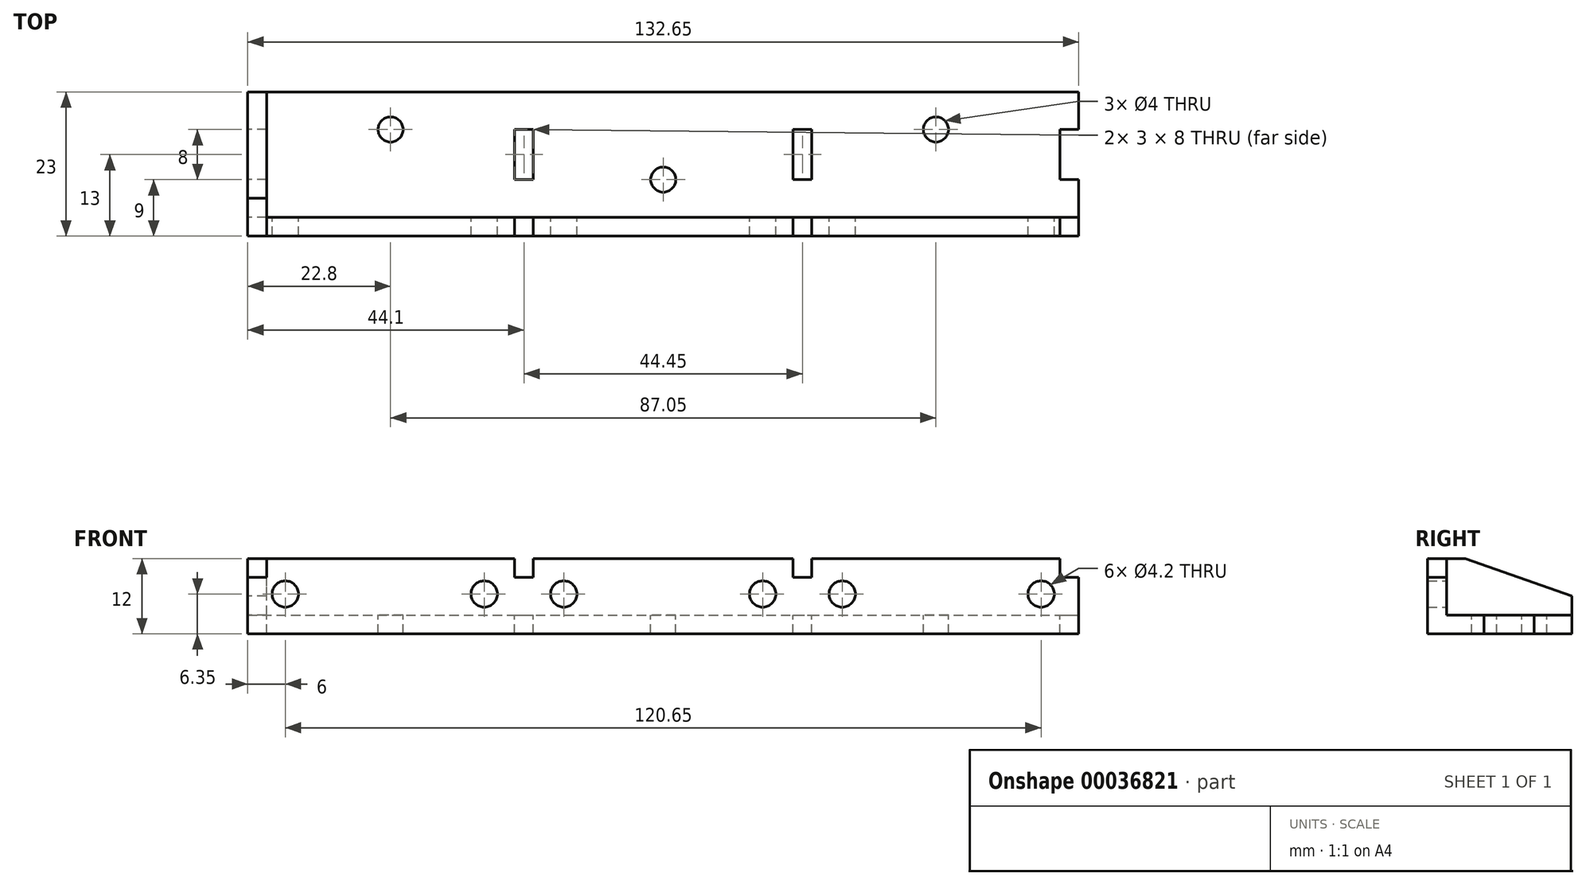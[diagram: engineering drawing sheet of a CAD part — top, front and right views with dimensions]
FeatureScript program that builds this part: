
annotation { "Feature Type Name" : "Feature", "Feature Type Description" : "" }
export const myFeature = defineFeature(function(context is Context, id is Id, definition is map)
    precondition{}
    {
        {
            var Q0;
            Q0=qCreatedBy(makeId("Front.planeOp"),FACE);
            var sketch = newSketch(context, id + "F0", { "sketchPlane" : qUnion([Q0])});
            skLineSegment(sketch, "E0.bottom", {"start": v(0, 0) * mm, "end": v(132.65, 0) * mm});
            skLineSegment(sketch, "E0.top", {"start": v(0, 12) * mm, "end": v(132.65, 12) * mm});
            skLineSegment(sketch, "E0.left", {"start": v(0, 0) * mm, "end": v(0, 12) * mm});
            skCircle(sketch, "E1", {"center": v(6, 6.35) * mm, "radius": 2.1 * mm});
            skCircle(sketch, "E2", {"center": v(37.75, 6.35) * mm, "radius": 2.1 * mm});
            skCircle(sketch, "E3", {"center": v(50.45, 6.35) * mm, "radius": 2.1 * mm});
            skCircle(sketch, "E4", {"center": v(82.2, 6.35) * mm, "radius": 2.1 * mm});
            skCircle(sketch, "E5", {"center": v(94.9, 6.35) * mm, "radius": 2.1 * mm});
            skCircle(sketch, "E6", {"center": v(126.65, 6.35) * mm, "radius": 2.1 * mm});
            skLineSegment(sketch, "E7", {"start": v(6, 6.35) * mm, "end": v(37.75, 6.35) * mm, "construction": true});
            skLineSegment(sketch, "E8", {"start": v(50.45, 6.35) * mm, "end": v(82.2, 6.35) * mm, "construction": true});
            skLineSegment(sketch, "E9", {"start": v(94.9, 6.35) * mm, "end": v(126.65, 6.35) * mm, "construction": true});
            skLineSegment(sketch, "E10", {"start": v(37.75, 6.35) * mm, "end": v(50.45, 6.35) * mm, "construction": true});
            skLineSegment(sketch, "E11", {"start": v(82.2, 6.35) * mm, "end": v(94.9, 6.35) * mm, "construction": true});
            skLineSegment(sketch, "E12", {"start": v(6, 6.35) * mm, "end": v(0, 6.35) * mm, "construction": true});
            skPoint(sketch, "E13", {"position": v(44.1, 6.35) * mm});
            skPoint(sketch, "E14", {"position": v(88.55, 6.35) * mm});
            skCircle(sketch, "E15", {"center": v(50.45, 6.35) * mm, "radius": 2.5 * mm, "construction": true});
            skLineSegment(sketch, "E16", {"start": v(132.65, 12) * mm, "end": v(132.65, 0) * mm});
            skLineSegment(sketch, "E17", {"start": v(126.65, 6.35) * mm, "end": v(132.65, 6.35) * mm, "construction": true});
            skSolve(sketch);
        }
        {
            var Q0;
            Q0=makeQuery(id+"F0.imprint","IMPRINT",FACE,{"disambiguationData":[TD([[makeQuery(id+"F0.imprint","IMPRINT",EDGE,{"derivedFrom":sQuery(id+"F0.wireOp",EDGE,"E0.bottom")}),1.0]])]});
            var sketch = newSketch(context, id + "F1", { "sketchPlane" : qUnion([Q0])});
            skLineSegment(sketch, "E18.bottom", {"start": v(6, 0) * mm, "end": v(9, 0) * mm});
            skLineSegment(sketch, "E18.top", {"start": v(6, 3) * mm, "end": v(9, 3) * mm});
            skLineSegment(sketch, "E18.left", {"start": v(6, 0) * mm, "end": v(6, 3) * mm});
            skLineSegment(sketch, "E18.right", {"start": v(9, 0) * mm, "end": v(9, 3) * mm});
            skLineSegment(sketch, "E19.bottom", {"start": v(11.75, 0) * mm, "end": v(14.75, 0) * mm});
            skLineSegment(sketch, "E19.top", {"start": v(11.75, 3) * mm, "end": v(14.75, 3) * mm});
            skLineSegment(sketch, "E19.left", {"start": v(11.75, 0) * mm, "end": v(11.75, 3) * mm});
            skLineSegment(sketch, "E19.right", {"start": v(14.75, 0) * mm, "end": v(14.75, 3) * mm});
            skLineSegment(sketch, "E20.bottom", {"start": v(17.5, 0) * mm, "end": v(20.5, 0) * mm});
            skLineSegment(sketch, "E20.top", {"start": v(17.5, 3) * mm, "end": v(20.5, 3) * mm});
            skLineSegment(sketch, "E20.left", {"start": v(17.5, 0) * mm, "end": v(17.5, 3) * mm});
            skLineSegment(sketch, "E20.right", {"start": v(20.5, 0) * mm, "end": v(20.5, 3) * mm});
            skLineSegment(sketch, "E21", {"start": v(9, 3) * mm, "end": v(11.75, 3) * mm, "construction": true});
            skLineSegment(sketch, "E22", {"start": v(14.75, 3) * mm, "end": v(17.5, 3) * mm, "construction": true});
            skLineSegment(sketch, "E23.bottom", {"start": v(23.25, 0) * mm, "end": v(26.25, 0) * mm});
            skLineSegment(sketch, "E23.top", {"start": v(23.25, 3) * mm, "end": v(26.25, 3) * mm});
            skLineSegment(sketch, "E23.left", {"start": v(23.25, 0) * mm, "end": v(23.25, 3) * mm});
            skLineSegment(sketch, "E23.right", {"start": v(26.25, 0) * mm, "end": v(26.25, 3) * mm});
            skLineSegment(sketch, "E24.bottom", {"start": v(29, 0) * mm, "end": v(32, 0) * mm});
            skLineSegment(sketch, "E24.top", {"start": v(29, 3) * mm, "end": v(32, 3) * mm});
            skLineSegment(sketch, "E24.left", {"start": v(29, 0) * mm, "end": v(29, 3) * mm});
            skLineSegment(sketch, "E24.right", {"start": v(32, 0) * mm, "end": v(32, 3) * mm});
            skLineSegment(sketch, "E25.bottom", {"start": v(34.75, 0) * mm, "end": v(37.75, 0) * mm});
            skLineSegment(sketch, "E25.top", {"start": v(34.75, 3) * mm, "end": v(37.75, 3) * mm});
            skLineSegment(sketch, "E25.left", {"start": v(34.75, 0) * mm, "end": v(34.75, 3) * mm});
            skLineSegment(sketch, "E25.right", {"start": v(37.75, 0) * mm, "end": v(37.75, 3) * mm});
            skLineSegment(sketch, "E26", {"start": v(20.5, 3) * mm, "end": v(23.25, 3) * mm, "construction": true});
            skLineSegment(sketch, "E27", {"start": v(26.25, 3) * mm, "end": v(29, 3) * mm, "construction": true});
            skLineSegment(sketch, "E28", {"start": v(32, 3) * mm, "end": v(34.75, 3) * mm, "construction": true});
            skLineSegment(sketch, "E29", {"start": v(44.1, 6.35) * mm, "end": v(44.1, 0) * mm, "construction": true});
            skLineSegment(sketch, "E30.MirrorCS", {"start": v(61.95, 3) * mm, "end": v(59.2, 3) * mm, "construction": true});
            skLineSegment(sketch, "E31.MirrorCS", {"start": v(76.45, 0) * mm, "end": v(73.45, 0) * mm});
            skLineSegment(sketch, "E32.MirrorCS", {"start": v(50.45, 0) * mm, "end": v(50.45, 3) * mm});
            skLineSegment(sketch, "E33.MirrorCS", {"start": v(53.45, 0) * mm, "end": v(53.45, 3) * mm});
            skLineSegment(sketch, "E34.MirrorCS", {"start": v(61.95, 0) * mm, "end": v(61.95, 3) * mm});
            skLineSegment(sketch, "E35.MirrorCS", {"start": v(79.2, 3) * mm, "end": v(76.45, 3) * mm, "construction": true});
            skLineSegment(sketch, "E36.MirrorCS", {"start": v(70.7, 0) * mm, "end": v(70.7, 3) * mm});
            skLineSegment(sketch, "E37.MirrorCS", {"start": v(59.2, 3) * mm, "end": v(56.2, 3) * mm});
            skLineSegment(sketch, "E38.MirrorCS", {"start": v(67.7, 0) * mm, "end": v(67.7, 3) * mm});
            skLineSegment(sketch, "E39.MirrorCS", {"start": v(64.95, 0) * mm, "end": v(64.95, 3) * mm});
            skLineSegment(sketch, "E40.MirrorCS", {"start": v(67.7, 3) * mm, "end": v(64.95, 3) * mm, "construction": true});
            skLineSegment(sketch, "E41.MirrorCS", {"start": v(82.2, 0) * mm, "end": v(79.2, 0) * mm});
            skLineSegment(sketch, "E42.MirrorCS", {"start": v(64.95, 0) * mm, "end": v(61.95, 0) * mm});
            skLineSegment(sketch, "E43.MirrorCS", {"start": v(53.45, 0) * mm, "end": v(50.45, 0) * mm});
            skLineSegment(sketch, "E44.MirrorCS", {"start": v(73.45, 0) * mm, "end": v(73.45, 3) * mm});
            skLineSegment(sketch, "E45.MirrorCS", {"start": v(82.2, 0) * mm, "end": v(82.2, 3) * mm});
            skLineSegment(sketch, "E46.MirrorCS", {"start": v(56.2, 0) * mm, "end": v(56.2, 3) * mm});
            skLineSegment(sketch, "E47.MirrorCS", {"start": v(53.45, 3) * mm, "end": v(50.45, 3) * mm});
            skLineSegment(sketch, "E48.MirrorCS", {"start": v(64.95, 3) * mm, "end": v(61.95, 3) * mm});
            skLineSegment(sketch, "E49.MirrorCS", {"start": v(59.2, 0) * mm, "end": v(56.2, 0) * mm});
            skLineSegment(sketch, "E50.MirrorCS", {"start": v(70.7, 3) * mm, "end": v(67.7, 3) * mm});
            skLineSegment(sketch, "E51.MirrorCS", {"start": v(70.7, 0) * mm, "end": v(67.7, 0) * mm});
            skLineSegment(sketch, "E52.MirrorCS", {"start": v(76.45, 3) * mm, "end": v(73.45, 3) * mm});
            skLineSegment(sketch, "E53.MirrorCS", {"start": v(56.2, 3) * mm, "end": v(53.45, 3) * mm, "construction": true});
            skLineSegment(sketch, "E54.MirrorCS", {"start": v(73.45, 3) * mm, "end": v(70.7, 3) * mm, "construction": true});
            skLineSegment(sketch, "E55.MirrorCS", {"start": v(79.2, 0) * mm, "end": v(79.2, 3) * mm});
            skLineSegment(sketch, "E56.MirrorCS", {"start": v(82.2, 3) * mm, "end": v(79.2, 3) * mm});
            skLineSegment(sketch, "E57.MirrorCS", {"start": v(59.2, 0) * mm, "end": v(59.2, 3) * mm});
            skLineSegment(sketch, "E58.MirrorCS", {"start": v(76.45, 0) * mm, "end": v(76.45, 3) * mm});
            skLineSegment(sketch, "E59", {"start": v(88.55, 6.35) * mm, "end": v(88.55, 0) * mm, "construction": true});
            skLineSegment(sketch, "E60.MirrorCS", {"start": v(97.9, 3) * mm, "end": v(100.65, 3) * mm, "construction": true});
            skLineSegment(sketch, "E61.MirrorCS", {"start": v(106.4, 3) * mm, "end": v(109.4, 3) * mm});
            skLineSegment(sketch, "E62.MirrorCS", {"start": v(109.4, 3) * mm, "end": v(112.15, 3) * mm, "construction": true});
            skLineSegment(sketch, "E63.MirrorCS", {"start": v(115.15, 3) * mm, "end": v(117.9, 3) * mm, "construction": true});
            skLineSegment(sketch, "E64.MirrorCS", {"start": v(103.65, 3) * mm, "end": v(106.4, 3) * mm, "construction": true});
            skLineSegment(sketch, "E65.MirrorCS", {"start": v(100.65, 3) * mm, "end": v(103.65, 3) * mm});
            skLineSegment(sketch, "E66.MirrorCS", {"start": v(112.15, 3) * mm, "end": v(115.15, 3) * mm});
            skLineSegment(sketch, "E67.MirrorCS", {"start": v(120.9, 3) * mm, "end": v(123.65, 3) * mm, "construction": true});
            skLineSegment(sketch, "E68.MirrorCS", {"start": v(117.9, 3) * mm, "end": v(120.9, 3) * mm});
            skLineSegment(sketch, "E69.MirrorCS", {"start": v(106.4, 0) * mm, "end": v(109.4, 0) * mm});
            skLineSegment(sketch, "E70.MirrorCS", {"start": v(112.15, 0) * mm, "end": v(115.15, 0) * mm});
            skLineSegment(sketch, "E71.MirrorCS", {"start": v(100.65, 0) * mm, "end": v(100.65, 3) * mm});
            skLineSegment(sketch, "E72.MirrorCS", {"start": v(115.15, 0) * mm, "end": v(115.15, 3) * mm});
            skLineSegment(sketch, "E73.MirrorCS", {"start": v(94.9, 0) * mm, "end": v(97.9, 0) * mm});
            skLineSegment(sketch, "E74.MirrorCS", {"start": v(117.9, 0) * mm, "end": v(117.9, 3) * mm});
            skLineSegment(sketch, "E75.MirrorCS", {"start": v(123.65, 0) * mm, "end": v(123.65, 3) * mm});
            skLineSegment(sketch, "E76.MirrorCS", {"start": v(117.9, 0) * mm, "end": v(120.9, 0) * mm});
            skLineSegment(sketch, "E77.MirrorCS", {"start": v(94.9, 3) * mm, "end": v(97.9, 3) * mm});
            skLineSegment(sketch, "E78.MirrorCS", {"start": v(120.9, 0) * mm, "end": v(120.9, 3) * mm});
            skLineSegment(sketch, "E79.MirrorCS", {"start": v(94.9, 0) * mm, "end": v(94.9, 3) * mm});
            skLineSegment(sketch, "E80.MirrorCS", {"start": v(126.65, 0) * mm, "end": v(126.65, 3) * mm});
            skLineSegment(sketch, "E81.MirrorCS", {"start": v(112.15, 0) * mm, "end": v(112.15, 3) * mm});
            skLineSegment(sketch, "E82.MirrorCS", {"start": v(123.65, 3) * mm, "end": v(126.65, 3) * mm});
            skLineSegment(sketch, "E83.MirrorCS", {"start": v(106.4, 0) * mm, "end": v(106.4, 3) * mm});
            skLineSegment(sketch, "E84.MirrorCS", {"start": v(97.9, 0) * mm, "end": v(97.9, 3) * mm});
            skLineSegment(sketch, "E85.MirrorCS", {"start": v(123.65, 0) * mm, "end": v(126.65, 0) * mm});
            skLineSegment(sketch, "E86.MirrorCS", {"start": v(103.65, 0) * mm, "end": v(103.65, 3) * mm});
            skLineSegment(sketch, "E87.MirrorCS", {"start": v(100.65, 0) * mm, "end": v(103.65, 0) * mm});
            skLineSegment(sketch, "E88.MirrorCS", {"start": v(109.4, 0) * mm, "end": v(109.4, 3) * mm});
            skLineSegment(sketch, "E89.bottom", {"start": v(0, 0) * mm, "end": v(3, 0) * mm});
            skLineSegment(sketch, "E89.top", {"start": v(0, 3) * mm, "end": v(3, 3) * mm});
            skLineSegment(sketch, "E89.left", {"start": v(0, 0) * mm, "end": v(0, 3) * mm});
            skLineSegment(sketch, "E89.right", {"start": v(3, 0) * mm, "end": v(3, 3) * mm});
            skLineSegment(sketch, "E90.bottom", {"start": v(42.6, 0) * mm, "end": v(45.6, 0) * mm});
            skLineSegment(sketch, "E90.top", {"start": v(42.6, 3) * mm, "end": v(45.6, 3) * mm});
            skLineSegment(sketch, "E90.left", {"start": v(42.6, 0) * mm, "end": v(42.6, 3) * mm});
            skLineSegment(sketch, "E90.right", {"start": v(45.6, 0) * mm, "end": v(45.6, 3) * mm});
            skLineSegment(sketch, "E91.bottom", {"start": v(87.05, 0) * mm, "end": v(90.05, 0) * mm});
            skLineSegment(sketch, "E91.top", {"start": v(87.05, 3) * mm, "end": v(90.05, 3) * mm});
            skLineSegment(sketch, "E91.left", {"start": v(87.05, 0) * mm, "end": v(87.05, 3) * mm});
            skLineSegment(sketch, "E91.right", {"start": v(90.05, 0) * mm, "end": v(90.05, 3) * mm});
            skPoint(sketch, "E92", {"position": v(44.1, 0) * mm});
            skPoint(sketch, "E93", {"position": v(88.55, 0) * mm});
            skLineSegment(sketch, "E94.bottom", {"start": v(132.65, 0) * mm, "end": v(129.65, 0) * mm});
            skLineSegment(sketch, "E94.top", {"start": v(132.65, 3) * mm, "end": v(129.65, 3) * mm});
            skLineSegment(sketch, "E94.left", {"start": v(132.65, 0) * mm, "end": v(132.65, 3) * mm});
            skLineSegment(sketch, "E94.right", {"start": v(129.65, 0) * mm, "end": v(129.65, 3) * mm});
            skSolve(sketch);
        }
        {
            var Q0;
            Q0=qCreatedBy(makeId("Front.planeOp"),FACE);
            var sketch = newSketch(context, id + "F2", { "sketchPlane" : qUnion([Q0])});
            skLineSegment(sketch, "E95.bottom", {"start": v(0, 0) * mm, "end": v(132.65, 0) * mm});
            skLineSegment(sketch, "E95.top", {"start": v(0, 3) * mm, "end": v(132.65, 3) * mm});
            skLineSegment(sketch, "E95.left", {"start": v(0, 0) * mm, "end": v(0, 3) * mm});
            skLineSegment(sketch, "E95.right", {"start": v(132.65, 0) * mm, "end": v(132.65, 3) * mm});
            skSolve(sketch);
        }
        {
            var Q0;
            Q0=qSketchRegion(id+"F0",true);
            extrude(context, id + "F3", {"entities" : qUnion([Q0]), "depth" : 3 * mm});
        }
        {
            var Q0;
            Q0=makeQuery(id+"F1.imprint","IMPRINT",FACE,{"disambiguationData":[TD([[makeQuery(id+"F1.imprint","IMPRINT",EDGE,{"derivedFrom":sQuery(id+"F1.wireOp",EDGE,"E89.bottom")}),1.0]])]});
            var Q1;
            Q1=makeQuery(id+"F1.imprint","IMPRINT",FACE,{"disambiguationData":[TD([[makeQuery(id+"F1.imprint","IMPRINT",EDGE,{"derivedFrom":sQuery(id+"F1.wireOp",EDGE,"E18.bottom")}),1.0]])]});
            var Q2;
            Q2=makeQuery(id+"F1.imprint","IMPRINT",FACE,{"disambiguationData":[TD([[makeQuery(id+"F1.imprint","IMPRINT",EDGE,{"derivedFrom":sQuery(id+"F1.wireOp",EDGE,"E19.bottom")}),1.0]])]});
            var Q3;
            Q3=makeQuery(id+"F1.imprint","IMPRINT",FACE,{"disambiguationData":[TD([[makeQuery(id+"F1.imprint","IMPRINT",EDGE,{"derivedFrom":sQuery(id+"F1.wireOp",EDGE,"E20.bottom")}),1.0]])]});
            var Q4;
            Q4=makeQuery(id+"F1.imprint","IMPRINT",FACE,{"disambiguationData":[TD([[makeQuery(id+"F1.imprint","IMPRINT",EDGE,{"derivedFrom":sQuery(id+"F1.wireOp",EDGE,"E23.bottom")}),1.0]])]});
            var Q5;
            Q5=makeQuery(id+"F1.imprint","IMPRINT",FACE,{"disambiguationData":[TD([[makeQuery(id+"F1.imprint","IMPRINT",EDGE,{"derivedFrom":sQuery(id+"F1.wireOp",EDGE,"E24.bottom")}),1.0]])]});
            var Q6;
            Q6=makeQuery(id+"F1.imprint","IMPRINT",FACE,{"disambiguationData":[TD([[makeQuery(id+"F1.imprint","IMPRINT",EDGE,{"derivedFrom":sQuery(id+"F1.wireOp",EDGE,"E25.bottom")}),1.0]])]});
            var Q7;
            Q7=makeQuery(id+"F1.imprint","IMPRINT",FACE,{"disambiguationData":[TD([[makeQuery(id+"F1.imprint","IMPRINT",EDGE,{"derivedFrom":sQuery(id+"F1.wireOp",EDGE,"E90.bottom")}),1.0]])]});
            var Q8;
            Q8=makeQuery(id+"F1.imprint","IMPRINT",FACE,{"disambiguationData":[TD([[makeQuery(id+"F1.imprint","IMPRINT",EDGE,{"derivedFrom":sQuery(id+"F1.wireOp",EDGE,"E32.MirrorCS")}),-1.0]])]});
            var Q9;
            Q9=makeQuery(id+"F1.imprint","IMPRINT",FACE,{"disambiguationData":[TD([[makeQuery(id+"F1.imprint","IMPRINT",EDGE,{"derivedFrom":sQuery(id+"F1.wireOp",EDGE,"E37.MirrorCS")}),1.0]])]});
            var Q10;
            Q10=makeQuery(id+"F1.imprint","IMPRINT",FACE,{"disambiguationData":[TD([[makeQuery(id+"F1.imprint","IMPRINT",EDGE,{"derivedFrom":sQuery(id+"F1.wireOp",EDGE,"E34.MirrorCS")}),-1.0]])]});
            var Q11;
            Q11=makeQuery(id+"F1.imprint","IMPRINT",FACE,{"disambiguationData":[TD([[makeQuery(id+"F1.imprint","IMPRINT",EDGE,{"derivedFrom":sQuery(id+"F1.wireOp",EDGE,"E36.MirrorCS")}),1.0]])]});
            var Q12;
            Q12=makeQuery(id+"F1.imprint","IMPRINT",FACE,{"disambiguationData":[TD([[makeQuery(id+"F1.imprint","IMPRINT",EDGE,{"derivedFrom":sQuery(id+"F1.wireOp",EDGE,"E31.MirrorCS")}),1.0]])]});
            var Q13;
            Q13=makeQuery(id+"F1.imprint","IMPRINT",FACE,{"disambiguationData":[TD([[makeQuery(id+"F1.imprint","IMPRINT",EDGE,{"derivedFrom":sQuery(id+"F1.wireOp",EDGE,"E41.MirrorCS")}),1.0]])]});
            var Q14;
            Q14=makeQuery(id+"F1.imprint","IMPRINT",FACE,{"disambiguationData":[TD([[makeQuery(id+"F1.imprint","IMPRINT",EDGE,{"derivedFrom":sQuery(id+"F1.wireOp",EDGE,"E91.bottom")}),1.0]])]});
            var Q15;
            Q15=makeQuery(id+"F1.imprint","IMPRINT",FACE,{"disambiguationData":[TD([[makeQuery(id+"F1.imprint","IMPRINT",EDGE,{"derivedFrom":sQuery(id+"F1.wireOp",EDGE,"E73.MirrorCS")}),1.0]])]});
            var Q16;
            Q16=makeQuery(id+"F1.imprint","IMPRINT",FACE,{"disambiguationData":[TD([[makeQuery(id+"F1.imprint","IMPRINT",EDGE,{"derivedFrom":sQuery(id+"F1.wireOp",EDGE,"E65.MirrorCS")}),-1.0]])]});
            var Q17;
            Q17=makeQuery(id+"F1.imprint","IMPRINT",FACE,{"disambiguationData":[TD([[makeQuery(id+"F1.imprint","IMPRINT",EDGE,{"derivedFrom":sQuery(id+"F1.wireOp",EDGE,"E61.MirrorCS")}),-1.0]])]});
            var Q18;
            Q18=makeQuery(id+"F1.imprint","IMPRINT",FACE,{"disambiguationData":[TD([[makeQuery(id+"F1.imprint","IMPRINT",EDGE,{"derivedFrom":sQuery(id+"F1.wireOp",EDGE,"E66.MirrorCS")}),-1.0]])]});
            var Q19;
            Q19=makeQuery(id+"F1.imprint","IMPRINT",FACE,{"disambiguationData":[TD([[makeQuery(id+"F1.imprint","IMPRINT",EDGE,{"derivedFrom":sQuery(id+"F1.wireOp",EDGE,"E68.MirrorCS")}),-1.0]])]});
            var Q20;
            Q20=makeQuery(id+"F1.imprint","IMPRINT",FACE,{"disambiguationData":[TD([[makeQuery(id+"F1.imprint","IMPRINT",EDGE,{"derivedFrom":sQuery(id+"F1.wireOp",EDGE,"E75.MirrorCS")}),-1.0]])]});
            var Q21;
            Q21=makeQuery(id+"F1.imprint","IMPRINT",FACE,{"disambiguationData":[TD([[makeQuery(id+"F1.imprint","IMPRINT",EDGE,{"derivedFrom":sQuery(id+"F1.wireOp",EDGE,"d6889f29-3aff-4a43-887b-f05846102f70.bottom")}),1.0]])]});
            var Q22;
            Q22=makeQuery(id+"F1.imprint","IMPRINT",FACE,{"disambiguationData":[TD([[makeQuery(id+"F1.imprint","IMPRINT",EDGE,{"derivedFrom":sQuery(id+"F1.wireOp",EDGE,"3edb70b5-b804-4be9-ab85-b3a438d2129227.MirrorCS")}),1.0]])]});
            var Q23;
            Q23=makeQuery(id+"F1.imprint","IMPRINT",FACE,{"disambiguationData":[TD([[makeQuery(id+"F1.imprint","IMPRINT",EDGE,{"derivedFrom":sQuery(id+"F1.wireOp",EDGE,"3edb70b5-b804-4be9-ab85-b3a438d212923.MirrorCS")}),1.0]])]});
            var Q24;
            Q24=makeQuery(id+"F1.imprint","IMPRINT",FACE,{"disambiguationData":[TD([[makeQuery(id+"F1.imprint","IMPRINT",EDGE,{"derivedFrom":sQuery(id+"F1.wireOp",EDGE,"3edb70b5-b804-4be9-ab85-b3a438d2129214.MirrorCS")}),1.0]])]});
            var Q25;
            Q25=makeQuery(id+"F1.imprint","IMPRINT",FACE,{"disambiguationData":[TD([[makeQuery(id+"F1.imprint","IMPRINT",EDGE,{"derivedFrom":sQuery(id+"F1.wireOp",EDGE,"3edb70b5-b804-4be9-ab85-b3a438d212922.MirrorCS")}),1.0]])]});
            var Q26;
            Q26=makeQuery(id+"F1.imprint","IMPRINT",FACE,{"disambiguationData":[TD([[makeQuery(id+"F1.imprint","IMPRINT",EDGE,{"derivedFrom":sQuery(id+"F1.wireOp",EDGE,"3edb70b5-b804-4be9-ab85-b3a438d2129216.MirrorCS")}),1.0]])]});
            var Q27;
            Q27=makeQuery(id+"F1.imprint","IMPRINT",FACE,{"disambiguationData":[TD([[makeQuery(id+"F1.imprint","IMPRINT",EDGE,{"derivedFrom":sQuery(id+"F1.wireOp",EDGE,"3edb70b5-b804-4be9-ab85-b3a438d2129232.MirrorCS")}),-1.0]])]});
            var Q28;
            {var subQ3=sQuery(id+"F1.wireOp",EDGE,"767c3735-2e18-495c-a88c-5e601239b8bc.left");Q28=makeQuery(id+"F1.imprint","IMPRINT",FACE,{"disambiguationData":[TD([[makeQuery(id+"F1.imprint","IMPRINT",EDGE,{"derivedFrom":subQ3}),-1.0]])]});}
            var Q29;
            {var subQ0=sQuery(id+"F1.wireOp",EDGE,"767c3735-2e18-495c-a88c-5e601239b8bc.right");Q29=makeQuery(id+"F1.imprint","IMPRINT",FACE,{"disambiguationData":[TD([[makeQuery(id+"F1.imprint","IMPRINT",EDGE,{"derivedFrom":subQ0}),1.0]])]});}
            var Q30;
            Q30=makeQuery(id+"F1.imprint","IMPRINT",FACE,{"disambiguationData":[TD([[makeQuery(id+"F1.imprint","IMPRINT",EDGE,{"derivedFrom":sQuery(id+"F1.wireOp",EDGE,"3edb70b5-b804-4be9-ab85-b3a438d2129229.MirrorCS")}),-1.0]])]});
            var Q31;
            Q31=makeQuery(id+"F1.imprint","IMPRINT",FACE,{"disambiguationData":[TD([[makeQuery(id+"F1.imprint","IMPRINT",EDGE,{"derivedFrom":sQuery(id+"F1.wireOp",EDGE,"3edb70b5-b804-4be9-ab85-b3a438d212921.MirrorCS")}),-1.0]])]});
            var Q32;
            Q32=makeQuery(id+"F1.imprint","IMPRINT",FACE,{"disambiguationData":[TD([[makeQuery(id+"F1.imprint","IMPRINT",EDGE,{"derivedFrom":sQuery(id+"F1.wireOp",EDGE,"3edb70b5-b804-4be9-ab85-b3a438d2129215.MirrorCS")}),-1.0]])]});
            var Q33;
            Q33=makeQuery(id+"F1.imprint","IMPRINT",FACE,{"disambiguationData":[TD([[makeQuery(id+"F1.imprint","IMPRINT",EDGE,{"derivedFrom":sQuery(id+"F1.wireOp",EDGE,"3edb70b5-b804-4be9-ab85-b3a438d2129220.MirrorCS")}),-1.0]])]});
            var Q34;
            Q34=makeQuery(id+"F1.imprint","IMPRINT",FACE,{"disambiguationData":[TD([[makeQuery(id+"F1.imprint","IMPRINT",EDGE,{"derivedFrom":sQuery(id+"F1.wireOp",EDGE,"3edb70b5-b804-4be9-ab85-b3a438d212927.MirrorCS")}),-1.0]])]});
            var Q35;
            Q35=makeQuery(id+"F1.imprint","IMPRINT",FACE,{"disambiguationData":[TD([[makeQuery(id+"F1.imprint","IMPRINT",EDGE,{"derivedFrom":sQuery(id+"F1.wireOp",EDGE,"3edb70b5-b804-4be9-ab85-b3a438d2129228.MirrorCS")}),1.0]])]});
            var Q36;
            {var subQ3=sQuery(id+"F1.wireOp",EDGE,"543f3bcf-fd4b-4987-a5e7-407be729de0d0.MirrorCS");Q36=makeQuery(id+"F1.imprint","IMPRINT",FACE,{"disambiguationData":[TD([[makeQuery(id+"F1.imprint","IMPRINT",EDGE,{"derivedFrom":subQ3}),-1.0]])]});}
            var Q37;
            {var subQ1=sQuery(id+"F1.wireOp",EDGE,"ccf9539e-e2bb-4c1d-8ae2-5d85fc4c74a40.MirrorCS");Q37=makeQuery(id+"F1.imprint","IMPRINT",FACE,{"disambiguationData":[TD([[makeQuery(id+"F1.imprint","IMPRINT",EDGE,{"derivedFrom":subQ1}),1.0]])]});}
            var Q38;
            Q38=makeQuery(id+"F1.imprint","IMPRINT",FACE,{"disambiguationData":[TD([[makeQuery(id+"F1.imprint","IMPRINT",EDGE,{"derivedFrom":sQuery(id+"F1.wireOp",EDGE,"3edb70b5-b804-4be9-ab85-b3a438d2129251.MirrorCS")}),-1.0]])]});
            var Q39;
            Q39=makeQuery(id+"F1.imprint","IMPRINT",FACE,{"disambiguationData":[TD([[makeQuery(id+"F1.imprint","IMPRINT",EDGE,{"derivedFrom":sQuery(id+"F1.wireOp",EDGE,"3edb70b5-b804-4be9-ab85-b3a438d2129211.MirrorCS")}),1.0]])]});
            var Q40;
            Q40=makeQuery(id+"F1.imprint","IMPRINT",FACE,{"disambiguationData":[TD([[makeQuery(id+"F1.imprint","IMPRINT",EDGE,{"derivedFrom":sQuery(id+"F1.wireOp",EDGE,"3edb70b5-b804-4be9-ab85-b3a438d2129226.MirrorCS")}),1.0]])]});
            var Q41;
            Q41=makeQuery(id+"F1.imprint","IMPRINT",FACE,{"disambiguationData":[TD([[makeQuery(id+"F1.imprint","IMPRINT",EDGE,{"derivedFrom":sQuery(id+"F1.wireOp",EDGE,"3edb70b5-b804-4be9-ab85-b3a438d2129218.MirrorCS")}),1.0]])]});
            var Q42;
            Q42=makeQuery(id+"F1.imprint","IMPRINT",FACE,{"disambiguationData":[TD([[makeQuery(id+"F1.imprint","IMPRINT",EDGE,{"derivedFrom":sQuery(id+"F1.wireOp",EDGE,"3edb70b5-b804-4be9-ab85-b3a438d2129225.MirrorCS")}),1.0]])]});
            var Q43;
            Q43=makeQuery(id+"F1.imprint","IMPRINT",FACE,{"disambiguationData":[TD([[makeQuery(id+"F1.imprint","IMPRINT",EDGE,{"derivedFrom":sQuery(id+"F1.wireOp",EDGE,"3edb70b5-b804-4be9-ab85-b3a438d2129263.MirrorCS")}),-1.0]])]});
            var Q44;
            Q44=makeQuery(id+"F1.imprint","IMPRINT",FACE,{"disambiguationData":[TD([[makeQuery(id+"F1.imprint","IMPRINT",EDGE,{"derivedFrom":sQuery(id+"F1.wireOp",EDGE,"6148efe5-7769-4a6e-beb2-6f02e7a2884e0.MirrorCS")}),1.0]])]});
            var Q45;
            Q45=makeQuery(id+"F1.imprint","IMPRINT",FACE,{"disambiguationData":[TD([[makeQuery(id+"F1.imprint","IMPRINT",EDGE,{"derivedFrom":sQuery(id+"F1.wireOp",EDGE,"14cc3a12-7d66-4c02-94a9-419769d5725533.MirrorCS")}),-1.0]])]});
            var Q46;
            Q46=makeQuery(id+"F1.imprint","IMPRINT",FACE,{"disambiguationData":[TD([[makeQuery(id+"F1.imprint","IMPRINT",EDGE,{"derivedFrom":sQuery(id+"F1.wireOp",EDGE,"14cc3a12-7d66-4c02-94a9-419769d572550.MirrorCS")}),-1.0]])]});
            var Q47;
            Q47=makeQuery(id+"F1.imprint","IMPRINT",FACE,{"disambiguationData":[TD([[makeQuery(id+"F1.imprint","IMPRINT",EDGE,{"derivedFrom":sQuery(id+"F1.wireOp",EDGE,"14cc3a12-7d66-4c02-94a9-419769d572558.MirrorCS")}),-1.0]])]});
            var Q48;
            Q48=makeQuery(id+"F1.imprint","IMPRINT",FACE,{"disambiguationData":[TD([[makeQuery(id+"F1.imprint","IMPRINT",EDGE,{"derivedFrom":sQuery(id+"F1.wireOp",EDGE,"14cc3a12-7d66-4c02-94a9-419769d5725514.MirrorCS")}),-1.0]])]});
            var Q49;
            Q49=makeQuery(id+"F1.imprint","IMPRINT",FACE,{"disambiguationData":[TD([[makeQuery(id+"F1.imprint","IMPRINT",EDGE,{"derivedFrom":sQuery(id+"F1.wireOp",EDGE,"14cc3a12-7d66-4c02-94a9-419769d5725517.MirrorCS")}),-1.0]])]});
            var Q50;
            Q50=makeQuery(id+"F1.imprint","IMPRINT",FACE,{"disambiguationData":[TD([[makeQuery(id+"F1.imprint","IMPRINT",EDGE,{"derivedFrom":sQuery(id+"F1.wireOp",EDGE,"14cc3a12-7d66-4c02-94a9-419769d5725522.MirrorCS")}),-1.0]])]});
            var Q51;
            {var subQ1=sQuery(id+"F1.wireOp",EDGE,"64f74f13-c9d3-42ce-b6e6-9e83b05c69170.MirrorCS");Q51=makeQuery(id+"F1.imprint","IMPRINT",FACE,{"disambiguationData":[TD([[makeQuery(id+"F1.imprint","IMPRINT",EDGE,{"derivedFrom":subQ1}),-1.0]])]});}
            var Q52;
            {var subQ3=sQuery(id+"F1.wireOp",EDGE,"b25d534e-4642-4852-ae6d-545176e5d0d50.MirrorCS");Q52=makeQuery(id+"F1.imprint","IMPRINT",FACE,{"disambiguationData":[TD([[makeQuery(id+"F1.imprint","IMPRINT",EDGE,{"derivedFrom":subQ3}),1.0]])]});}
            var Q53;
            Q53=makeQuery(id+"F1.imprint","IMPRINT",FACE,{"disambiguationData":[TD([[makeQuery(id+"F1.imprint","IMPRINT",EDGE,{"derivedFrom":sQuery(id+"F1.wireOp",EDGE,"14cc3a12-7d66-4c02-94a9-419769d5725521.MirrorCS")}),1.0]])]});
            var Q54;
            Q54=makeQuery(id+"F1.imprint","IMPRINT",FACE,{"disambiguationData":[TD([[makeQuery(id+"F1.imprint","IMPRINT",EDGE,{"derivedFrom":sQuery(id+"F1.wireOp",EDGE,"14cc3a12-7d66-4c02-94a9-419769d572553.MirrorCS")}),1.0]])]});
            var Q55;
            Q55=makeQuery(id+"F1.imprint","IMPRINT",FACE,{"disambiguationData":[TD([[makeQuery(id+"F1.imprint","IMPRINT",EDGE,{"derivedFrom":sQuery(id+"F1.wireOp",EDGE,"14cc3a12-7d66-4c02-94a9-419769d572557.MirrorCS")}),1.0]])]});
            var Q56;
            Q56=makeQuery(id+"F1.imprint","IMPRINT",FACE,{"disambiguationData":[TD([[makeQuery(id+"F1.imprint","IMPRINT",EDGE,{"derivedFrom":sQuery(id+"F1.wireOp",EDGE,"14cc3a12-7d66-4c02-94a9-419769d5725512.MirrorCS")}),1.0]])]});
            var Q57;
            Q57=makeQuery(id+"F1.imprint","IMPRINT",FACE,{"disambiguationData":[TD([[makeQuery(id+"F1.imprint","IMPRINT",EDGE,{"derivedFrom":sQuery(id+"F1.wireOp",EDGE,"14cc3a12-7d66-4c02-94a9-419769d5725515.MirrorCS")}),1.0]])]});
            var Q58;
            Q58=makeQuery(id+"F1.imprint","IMPRINT",FACE,{"disambiguationData":[TD([[makeQuery(id+"F1.imprint","IMPRINT",EDGE,{"derivedFrom":sQuery(id+"F1.wireOp",EDGE,"14cc3a12-7d66-4c02-94a9-419769d5725527.MirrorCS")}),-1.0]])]});
            var Q59;
            Q59=makeQuery(id+"F1.imprint","IMPRINT",FACE,{"disambiguationData":[TD([[makeQuery(id+"F1.imprint","IMPRINT",EDGE,{"derivedFrom":sQuery(id+"F1.wireOp",EDGE,"2b8ea9ff-144e-4082-a664-a4dd3dd94e410.MirrorCS")}),1.0]])]});
            var Q60;
            {var subQ2=sQuery(id+"F1.wireOp",EDGE,"SqbHijmA-EvCf-u65W-CcwQ-tsmZO2ZK6Ml2");Q60=makeQuery(id+"F1.imprint","IMPRINT",FACE,{"disambiguationData":[TD([[makeQuery(id+"F1.imprint","IMPRINT",EDGE,{"derivedFrom":subQ2}),1.0]])]});}
            extrude(context, id + "F4", {"entities" : qUnion([Q0, Q1, Q2, Q3, Q4, Q5, Q6, Q7, Q8, Q9, Q10, Q11, Q12, Q13, Q14, Q15, Q16, Q17, Q18, Q19, Q20, Q21, Q22, Q23, Q24, Q25, Q26, Q27, Q28, Q29, Q30, Q31, Q32, Q33, Q34, Q35, Q36, Q37, Q38, Q39, Q40, Q41, Q42, Q43, Q44, Q45, Q46, Q47, Q48, Q49, Q50, Q51, Q52, Q53, Q54, Q55, Q56, Q57, Q58, Q59, Q60]), "operationType" : NewBodyOperationType.REMOVE, "endBound" : BoundingType.THROUGH_ALL, "depth" : 25 * mm});
        }
        {
            var Q0;
            Q0=makeQuery(id+"F2.imprint","IMPRINT",FACE,{"disambiguationData":[TD([[makeQuery(id+"F2.imprint","IMPRINT",EDGE,{"derivedFrom":sQuery(id+"F2.wireOp",EDGE,"E95.bottom")}),1.0]])]});
            extrude(context, id + "F5", {"entities" : qUnion([Q0]), "oppositeDirection" : true, "depth" : 20 * mm});
        }
        {
            var Q0;
            Q0=makeQuery(id+"F1.imprint","IMPRINT",FACE,{"disambiguationData":[TD([[makeQuery(id+"F1.imprint","IMPRINT",EDGE,{"derivedFrom":sQuery(id+"F1.wireOp",EDGE,"2b8ea9ff-144e-4082-a664-a4dd3dd94e410.MirrorCS")}),1.0]])]});
            var Q1;
            Q1=makeQuery(id+"F1.imprint","IMPRINT",FACE,{"disambiguationData":[TD([[makeQuery(id+"F1.imprint","IMPRINT",EDGE,{"derivedFrom":sQuery(id+"F1.wireOp",EDGE,"14cc3a12-7d66-4c02-94a9-419769d5725527.MirrorCS")}),-1.0]])]});
            var Q2;
            Q2=makeQuery(id+"F1.imprint","IMPRINT",FACE,{"disambiguationData":[TD([[makeQuery(id+"F1.imprint","IMPRINT",EDGE,{"derivedFrom":sQuery(id+"F1.wireOp",EDGE,"14cc3a12-7d66-4c02-94a9-419769d5725515.MirrorCS")}),1.0]])]});
            var Q3;
            Q3=makeQuery(id+"F1.imprint","IMPRINT",FACE,{"disambiguationData":[TD([[makeQuery(id+"F1.imprint","IMPRINT",EDGE,{"derivedFrom":sQuery(id+"F1.wireOp",EDGE,"14cc3a12-7d66-4c02-94a9-419769d5725512.MirrorCS")}),1.0]])]});
            var Q4;
            Q4=makeQuery(id+"F1.imprint","IMPRINT",FACE,{"disambiguationData":[TD([[makeQuery(id+"F1.imprint","IMPRINT",EDGE,{"derivedFrom":sQuery(id+"F1.wireOp",EDGE,"14cc3a12-7d66-4c02-94a9-419769d572557.MirrorCS")}),1.0]])]});
            var Q5;
            Q5=makeQuery(id+"F1.imprint","IMPRINT",FACE,{"disambiguationData":[TD([[makeQuery(id+"F1.imprint","IMPRINT",EDGE,{"derivedFrom":sQuery(id+"F1.wireOp",EDGE,"14cc3a12-7d66-4c02-94a9-419769d572553.MirrorCS")}),1.0]])]});
            var Q6;
            Q6=makeQuery(id+"F1.imprint","IMPRINT",FACE,{"disambiguationData":[TD([[makeQuery(id+"F1.imprint","IMPRINT",EDGE,{"derivedFrom":sQuery(id+"F1.wireOp",EDGE,"14cc3a12-7d66-4c02-94a9-419769d5725521.MirrorCS")}),1.0]])]});
            var Q7;
            {var subQ3=sQuery(id+"F1.wireOp",EDGE,"b25d534e-4642-4852-ae6d-545176e5d0d50.MirrorCS");Q7=makeQuery(id+"F1.imprint","IMPRINT",FACE,{"disambiguationData":[TD([[makeQuery(id+"F1.imprint","IMPRINT",EDGE,{"derivedFrom":subQ3}),1.0]])]});}
            var Q8;
            {var subQ1=sQuery(id+"F1.wireOp",EDGE,"64f74f13-c9d3-42ce-b6e6-9e83b05c69170.MirrorCS");Q8=makeQuery(id+"F1.imprint","IMPRINT",FACE,{"disambiguationData":[TD([[makeQuery(id+"F1.imprint","IMPRINT",EDGE,{"derivedFrom":subQ1}),-1.0]])]});}
            var Q9;
            Q9=makeQuery(id+"F1.imprint","IMPRINT",FACE,{"disambiguationData":[TD([[makeQuery(id+"F1.imprint","IMPRINT",EDGE,{"derivedFrom":sQuery(id+"F1.wireOp",EDGE,"14cc3a12-7d66-4c02-94a9-419769d5725522.MirrorCS")}),-1.0]])]});
            var Q10;
            Q10=makeQuery(id+"F1.imprint","IMPRINT",FACE,{"disambiguationData":[TD([[makeQuery(id+"F1.imprint","IMPRINT",EDGE,{"derivedFrom":sQuery(id+"F1.wireOp",EDGE,"14cc3a12-7d66-4c02-94a9-419769d5725517.MirrorCS")}),-1.0]])]});
            var Q11;
            Q11=makeQuery(id+"F1.imprint","IMPRINT",FACE,{"disambiguationData":[TD([[makeQuery(id+"F1.imprint","IMPRINT",EDGE,{"derivedFrom":sQuery(id+"F1.wireOp",EDGE,"14cc3a12-7d66-4c02-94a9-419769d5725514.MirrorCS")}),-1.0]])]});
            var Q12;
            Q12=makeQuery(id+"F1.imprint","IMPRINT",FACE,{"disambiguationData":[TD([[makeQuery(id+"F1.imprint","IMPRINT",EDGE,{"derivedFrom":sQuery(id+"F1.wireOp",EDGE,"14cc3a12-7d66-4c02-94a9-419769d572558.MirrorCS")}),-1.0]])]});
            var Q13;
            Q13=makeQuery(id+"F1.imprint","IMPRINT",FACE,{"disambiguationData":[TD([[makeQuery(id+"F1.imprint","IMPRINT",EDGE,{"derivedFrom":sQuery(id+"F1.wireOp",EDGE,"14cc3a12-7d66-4c02-94a9-419769d572550.MirrorCS")}),-1.0]])]});
            var Q14;
            Q14=makeQuery(id+"F1.imprint","IMPRINT",FACE,{"disambiguationData":[TD([[makeQuery(id+"F1.imprint","IMPRINT",EDGE,{"derivedFrom":sQuery(id+"F1.wireOp",EDGE,"14cc3a12-7d66-4c02-94a9-419769d5725533.MirrorCS")}),-1.0]])]});
            var Q15;
            Q15=makeQuery(id+"F1.imprint","IMPRINT",FACE,{"disambiguationData":[TD([[makeQuery(id+"F1.imprint","IMPRINT",EDGE,{"derivedFrom":sQuery(id+"F1.wireOp",EDGE,"6148efe5-7769-4a6e-beb2-6f02e7a2884e0.MirrorCS")}),1.0]])]});
            var Q16;
            Q16=makeQuery(id+"F1.imprint","IMPRINT",FACE,{"disambiguationData":[TD([[makeQuery(id+"F1.imprint","IMPRINT",EDGE,{"derivedFrom":sQuery(id+"F1.wireOp",EDGE,"3edb70b5-b804-4be9-ab85-b3a438d2129263.MirrorCS")}),-1.0]])]});
            var Q17;
            Q17=makeQuery(id+"F1.imprint","IMPRINT",FACE,{"disambiguationData":[TD([[makeQuery(id+"F1.imprint","IMPRINT",EDGE,{"derivedFrom":sQuery(id+"F1.wireOp",EDGE,"3edb70b5-b804-4be9-ab85-b3a438d2129225.MirrorCS")}),1.0]])]});
            var Q18;
            Q18=makeQuery(id+"F1.imprint","IMPRINT",FACE,{"disambiguationData":[TD([[makeQuery(id+"F1.imprint","IMPRINT",EDGE,{"derivedFrom":sQuery(id+"F1.wireOp",EDGE,"3edb70b5-b804-4be9-ab85-b3a438d2129218.MirrorCS")}),1.0]])]});
            var Q19;
            Q19=makeQuery(id+"F1.imprint","IMPRINT",FACE,{"disambiguationData":[TD([[makeQuery(id+"F1.imprint","IMPRINT",EDGE,{"derivedFrom":sQuery(id+"F1.wireOp",EDGE,"3edb70b5-b804-4be9-ab85-b3a438d2129226.MirrorCS")}),1.0]])]});
            var Q20;
            Q20=makeQuery(id+"F1.imprint","IMPRINT",FACE,{"disambiguationData":[TD([[makeQuery(id+"F1.imprint","IMPRINT",EDGE,{"derivedFrom":sQuery(id+"F1.wireOp",EDGE,"3edb70b5-b804-4be9-ab85-b3a438d2129211.MirrorCS")}),1.0]])]});
            var Q21;
            Q21=makeQuery(id+"F1.imprint","IMPRINT",FACE,{"disambiguationData":[TD([[makeQuery(id+"F1.imprint","IMPRINT",EDGE,{"derivedFrom":sQuery(id+"F1.wireOp",EDGE,"3edb70b5-b804-4be9-ab85-b3a438d2129251.MirrorCS")}),-1.0]])]});
            var Q22;
            {var subQ1=sQuery(id+"F1.wireOp",EDGE,"ccf9539e-e2bb-4c1d-8ae2-5d85fc4c74a40.MirrorCS");Q22=makeQuery(id+"F1.imprint","IMPRINT",FACE,{"disambiguationData":[TD([[makeQuery(id+"F1.imprint","IMPRINT",EDGE,{"derivedFrom":subQ1}),1.0]])]});}
            var Q23;
            {var subQ3=sQuery(id+"F1.wireOp",EDGE,"543f3bcf-fd4b-4987-a5e7-407be729de0d0.MirrorCS");Q23=makeQuery(id+"F1.imprint","IMPRINT",FACE,{"disambiguationData":[TD([[makeQuery(id+"F1.imprint","IMPRINT",EDGE,{"derivedFrom":subQ3}),-1.0]])]});}
            var Q24;
            Q24=makeQuery(id+"F1.imprint","IMPRINT",FACE,{"disambiguationData":[TD([[makeQuery(id+"F1.imprint","IMPRINT",EDGE,{"derivedFrom":sQuery(id+"F1.wireOp",EDGE,"3edb70b5-b804-4be9-ab85-b3a438d2129228.MirrorCS")}),1.0]])]});
            var Q25;
            Q25=makeQuery(id+"F1.imprint","IMPRINT",FACE,{"disambiguationData":[TD([[makeQuery(id+"F1.imprint","IMPRINT",EDGE,{"derivedFrom":sQuery(id+"F1.wireOp",EDGE,"3edb70b5-b804-4be9-ab85-b3a438d212927.MirrorCS")}),-1.0]])]});
            var Q26;
            Q26=makeQuery(id+"F1.imprint","IMPRINT",FACE,{"disambiguationData":[TD([[makeQuery(id+"F1.imprint","IMPRINT",EDGE,{"derivedFrom":sQuery(id+"F1.wireOp",EDGE,"3edb70b5-b804-4be9-ab85-b3a438d2129220.MirrorCS")}),-1.0]])]});
            var Q27;
            Q27=makeQuery(id+"F1.imprint","IMPRINT",FACE,{"disambiguationData":[TD([[makeQuery(id+"F1.imprint","IMPRINT",EDGE,{"derivedFrom":sQuery(id+"F1.wireOp",EDGE,"3edb70b5-b804-4be9-ab85-b3a438d2129215.MirrorCS")}),-1.0]])]});
            var Q28;
            Q28=makeQuery(id+"F1.imprint","IMPRINT",FACE,{"disambiguationData":[TD([[makeQuery(id+"F1.imprint","IMPRINT",EDGE,{"derivedFrom":sQuery(id+"F1.wireOp",EDGE,"3edb70b5-b804-4be9-ab85-b3a438d212921.MirrorCS")}),-1.0]])]});
            var Q29;
            Q29=makeQuery(id+"F1.imprint","IMPRINT",FACE,{"disambiguationData":[TD([[makeQuery(id+"F1.imprint","IMPRINT",EDGE,{"derivedFrom":sQuery(id+"F1.wireOp",EDGE,"3edb70b5-b804-4be9-ab85-b3a438d2129229.MirrorCS")}),-1.0]])]});
            var Q30;
            {var subQ0=sQuery(id+"F1.wireOp",EDGE,"767c3735-2e18-495c-a88c-5e601239b8bc.right");Q30=makeQuery(id+"F1.imprint","IMPRINT",FACE,{"disambiguationData":[TD([[makeQuery(id+"F1.imprint","IMPRINT",EDGE,{"derivedFrom":subQ0}),1.0]])]});}
            var Q31;
            {var subQ3=sQuery(id+"F1.wireOp",EDGE,"767c3735-2e18-495c-a88c-5e601239b8bc.left");Q31=makeQuery(id+"F1.imprint","IMPRINT",FACE,{"disambiguationData":[TD([[makeQuery(id+"F1.imprint","IMPRINT",EDGE,{"derivedFrom":subQ3}),-1.0]])]});}
            var Q32;
            Q32=makeQuery(id+"F1.imprint","IMPRINT",FACE,{"disambiguationData":[TD([[makeQuery(id+"F1.imprint","IMPRINT",EDGE,{"derivedFrom":sQuery(id+"F1.wireOp",EDGE,"3edb70b5-b804-4be9-ab85-b3a438d2129232.MirrorCS")}),-1.0]])]});
            var Q33;
            Q33=makeQuery(id+"F1.imprint","IMPRINT",FACE,{"disambiguationData":[TD([[makeQuery(id+"F1.imprint","IMPRINT",EDGE,{"derivedFrom":sQuery(id+"F1.wireOp",EDGE,"3edb70b5-b804-4be9-ab85-b3a438d2129216.MirrorCS")}),1.0]])]});
            var Q34;
            Q34=makeQuery(id+"F1.imprint","IMPRINT",FACE,{"disambiguationData":[TD([[makeQuery(id+"F1.imprint","IMPRINT",EDGE,{"derivedFrom":sQuery(id+"F1.wireOp",EDGE,"3edb70b5-b804-4be9-ab85-b3a438d212922.MirrorCS")}),1.0]])]});
            var Q35;
            Q35=makeQuery(id+"F1.imprint","IMPRINT",FACE,{"disambiguationData":[TD([[makeQuery(id+"F1.imprint","IMPRINT",EDGE,{"derivedFrom":sQuery(id+"F1.wireOp",EDGE,"3edb70b5-b804-4be9-ab85-b3a438d2129214.MirrorCS")}),1.0]])]});
            var Q36;
            Q36=makeQuery(id+"F1.imprint","IMPRINT",FACE,{"disambiguationData":[TD([[makeQuery(id+"F1.imprint","IMPRINT",EDGE,{"derivedFrom":sQuery(id+"F1.wireOp",EDGE,"3edb70b5-b804-4be9-ab85-b3a438d212923.MirrorCS")}),1.0]])]});
            var Q37;
            Q37=makeQuery(id+"F1.imprint","IMPRINT",FACE,{"disambiguationData":[TD([[makeQuery(id+"F1.imprint","IMPRINT",EDGE,{"derivedFrom":sQuery(id+"F1.wireOp",EDGE,"3edb70b5-b804-4be9-ab85-b3a438d2129227.MirrorCS")}),1.0]])]});
            var Q38;
            Q38=makeQuery(id+"F1.imprint","IMPRINT",FACE,{"disambiguationData":[TD([[makeQuery(id+"F1.imprint","IMPRINT",EDGE,{"derivedFrom":sQuery(id+"F1.wireOp",EDGE,"E75.MirrorCS")}),-1.0]])]});
            var Q39;
            Q39=makeQuery(id+"F1.imprint","IMPRINT",FACE,{"disambiguationData":[TD([[makeQuery(id+"F1.imprint","IMPRINT",EDGE,{"derivedFrom":sQuery(id+"F1.wireOp",EDGE,"E68.MirrorCS")}),-1.0]])]});
            var Q40;
            Q40=makeQuery(id+"F1.imprint","IMPRINT",FACE,{"disambiguationData":[TD([[makeQuery(id+"F1.imprint","IMPRINT",EDGE,{"derivedFrom":sQuery(id+"F1.wireOp",EDGE,"E66.MirrorCS")}),-1.0]])]});
            var Q41;
            Q41=makeQuery(id+"F1.imprint","IMPRINT",FACE,{"disambiguationData":[TD([[makeQuery(id+"F1.imprint","IMPRINT",EDGE,{"derivedFrom":sQuery(id+"F1.wireOp",EDGE,"E61.MirrorCS")}),-1.0]])]});
            var Q42;
            Q42=makeQuery(id+"F1.imprint","IMPRINT",FACE,{"disambiguationData":[TD([[makeQuery(id+"F1.imprint","IMPRINT",EDGE,{"derivedFrom":sQuery(id+"F1.wireOp",EDGE,"E65.MirrorCS")}),-1.0]])]});
            var Q43;
            Q43=makeQuery(id+"F1.imprint","IMPRINT",FACE,{"disambiguationData":[TD([[makeQuery(id+"F1.imprint","IMPRINT",EDGE,{"derivedFrom":sQuery(id+"F1.wireOp",EDGE,"E73.MirrorCS")}),1.0]])]});
            var Q44;
            Q44=makeQuery(id+"F1.imprint","IMPRINT",FACE,{"disambiguationData":[TD([[makeQuery(id+"F1.imprint","IMPRINT",EDGE,{"derivedFrom":sQuery(id+"F1.wireOp",EDGE,"d6889f29-3aff-4a43-887b-f05846102f70.bottom")}),1.0]])]});
            var Q45;
            Q45=makeQuery(id+"F1.imprint","IMPRINT",FACE,{"disambiguationData":[TD([[makeQuery(id+"F1.imprint","IMPRINT",EDGE,{"derivedFrom":sQuery(id+"F1.wireOp",EDGE,"E91.bottom")}),1.0]])]});
            var Q46;
            Q46=makeQuery(id+"F1.imprint","IMPRINT",FACE,{"disambiguationData":[TD([[makeQuery(id+"F1.imprint","IMPRINT",EDGE,{"derivedFrom":sQuery(id+"F1.wireOp",EDGE,"E41.MirrorCS")}),1.0]])]});
            var Q47;
            Q47=makeQuery(id+"F1.imprint","IMPRINT",FACE,{"disambiguationData":[TD([[makeQuery(id+"F1.imprint","IMPRINT",EDGE,{"derivedFrom":sQuery(id+"F1.wireOp",EDGE,"E31.MirrorCS")}),1.0]])]});
            var Q48;
            Q48=makeQuery(id+"F1.imprint","IMPRINT",FACE,{"disambiguationData":[TD([[makeQuery(id+"F1.imprint","IMPRINT",EDGE,{"derivedFrom":sQuery(id+"F1.wireOp",EDGE,"E36.MirrorCS")}),1.0]])]});
            var Q49;
            Q49=makeQuery(id+"F1.imprint","IMPRINT",FACE,{"disambiguationData":[TD([[makeQuery(id+"F1.imprint","IMPRINT",EDGE,{"derivedFrom":sQuery(id+"F1.wireOp",EDGE,"E34.MirrorCS")}),-1.0]])]});
            var Q50;
            Q50=makeQuery(id+"F1.imprint","IMPRINT",FACE,{"disambiguationData":[TD([[makeQuery(id+"F1.imprint","IMPRINT",EDGE,{"derivedFrom":sQuery(id+"F1.wireOp",EDGE,"E37.MirrorCS")}),1.0]])]});
            var Q51;
            Q51=makeQuery(id+"F1.imprint","IMPRINT",FACE,{"disambiguationData":[TD([[makeQuery(id+"F1.imprint","IMPRINT",EDGE,{"derivedFrom":sQuery(id+"F1.wireOp",EDGE,"E32.MirrorCS")}),-1.0]])]});
            var Q52;
            Q52=makeQuery(id+"F1.imprint","IMPRINT",FACE,{"disambiguationData":[TD([[makeQuery(id+"F1.imprint","IMPRINT",EDGE,{"derivedFrom":sQuery(id+"F1.wireOp",EDGE,"E90.bottom")}),1.0]])]});
            var Q53;
            Q53=makeQuery(id+"F1.imprint","IMPRINT",FACE,{"disambiguationData":[TD([[makeQuery(id+"F1.imprint","IMPRINT",EDGE,{"derivedFrom":sQuery(id+"F1.wireOp",EDGE,"E25.bottom")}),1.0]])]});
            var Q54;
            Q54=makeQuery(id+"F1.imprint","IMPRINT",FACE,{"disambiguationData":[TD([[makeQuery(id+"F1.imprint","IMPRINT",EDGE,{"derivedFrom":sQuery(id+"F1.wireOp",EDGE,"E24.bottom")}),1.0]])]});
            var Q55;
            Q55=makeQuery(id+"F1.imprint","IMPRINT",FACE,{"disambiguationData":[TD([[makeQuery(id+"F1.imprint","IMPRINT",EDGE,{"derivedFrom":sQuery(id+"F1.wireOp",EDGE,"E23.bottom")}),1.0]])]});
            var Q56;
            Q56=makeQuery(id+"F1.imprint","IMPRINT",FACE,{"disambiguationData":[TD([[makeQuery(id+"F1.imprint","IMPRINT",EDGE,{"derivedFrom":sQuery(id+"F1.wireOp",EDGE,"E20.bottom")}),1.0]])]});
            var Q57;
            Q57=makeQuery(id+"F1.imprint","IMPRINT",FACE,{"disambiguationData":[TD([[makeQuery(id+"F1.imprint","IMPRINT",EDGE,{"derivedFrom":sQuery(id+"F1.wireOp",EDGE,"E19.bottom")}),1.0]])]});
            var Q58;
            Q58=makeQuery(id+"F1.imprint","IMPRINT",FACE,{"disambiguationData":[TD([[makeQuery(id+"F1.imprint","IMPRINT",EDGE,{"derivedFrom":sQuery(id+"F1.wireOp",EDGE,"E18.bottom")}),1.0]])]});
            var Q59;
            Q59=makeQuery(id+"F1.imprint","IMPRINT",FACE,{"disambiguationData":[TD([[makeQuery(id+"F1.imprint","IMPRINT",EDGE,{"derivedFrom":sQuery(id+"F1.wireOp",EDGE,"E89.bottom")}),1.0]])]});
            var Q60;
            Q60=makeQuery(id+"F1.imprint","IMPRINT",FACE,{"disambiguationData":[TD([[makeQuery(id+"F1.imprint","IMPRINT",EDGE,{"derivedFrom":sQuery(id+"F1.wireOp",EDGE,"E94.bottom")}),1.0]])]});
            extrude(context, id + "F6", {"entities" : qUnion([Q0, Q1, Q2, Q3, Q4, Q5, Q6, Q7, Q8, Q9, Q10, Q11, Q12, Q13, Q14, Q15, Q16, Q17, Q18, Q19, Q20, Q21, Q22, Q23, Q24, Q25, Q26, Q27, Q28, Q29, Q30, Q31, Q32, Q33, Q34, Q35, Q36, Q37, Q38, Q39, Q40, Q41, Q42, Q43, Q44, Q45, Q46, Q47, Q48, Q49, Q50, Q51, Q52, Q53, Q54, Q55, Q56, Q57, Q58, Q59, Q60]), "operationType" : NewBodyOperationType.ADD, "depth" : 3 * mm});
        }
        {
            var Q0;
            Q0=makeQuery(id+"F6.boolean.opBoolean","MERGE",FACE,{"derivedFrom":[makeQuery(id+"F5.opExtrude","SWEPT_FACE",FACE,{"disambiguationData":[OSD([sQuery(id+"F2.wireOp",EDGE,"E95.top")])]}),makeQuery(id+"F6.opExtrude","SWEPT_FACE",FACE,{"disambiguationData":[OSD([sQuery(id+"F1.wireOp",EDGE,"E18.top")])]}),makeQuery(id+"F6.opExtrude","SWEPT_FACE",FACE,{"disambiguationData":[OSD([sQuery(id+"F1.wireOp",EDGE,"E19.top")])]}),makeQuery(id+"F6.opExtrude","SWEPT_FACE",FACE,{"disambiguationData":[OSD([sQuery(id+"F1.wireOp",EDGE,"E20.top")])]}),makeQuery(id+"F6.opExtrude","SWEPT_FACE",FACE,{"disambiguationData":[OSD([sQuery(id+"F1.wireOp",EDGE,"E23.top")])]}),makeQuery(id+"F6.opExtrude","SWEPT_FACE",FACE,{"disambiguationData":[OSD([sQuery(id+"F1.wireOp",EDGE,"E24.top")])]}),makeQuery(id+"F6.opExtrude","SWEPT_FACE",FACE,{"disambiguationData":[OSD([sQuery(id+"F1.wireOp",EDGE,"E25.top")])]}),makeQuery(id+"F6.opExtrude","SWEPT_FACE",FACE,{"disambiguationData":[OSD([sQuery(id+"F1.wireOp",EDGE,"E37.MirrorCS")])]}),makeQuery(id+"F6.opExtrude","SWEPT_FACE",FACE,{"disambiguationData":[OSD([sQuery(id+"F1.wireOp",EDGE,"E47.MirrorCS")])]}),makeQuery(id+"F6.opExtrude","SWEPT_FACE",FACE,{"disambiguationData":[OSD([sQuery(id+"F1.wireOp",EDGE,"E48.MirrorCS")])]}),makeQuery(id+"F6.opExtrude","SWEPT_FACE",FACE,{"disambiguationData":[OSD([sQuery(id+"F1.wireOp",EDGE,"E50.MirrorCS")])]}),makeQuery(id+"F6.opExtrude","SWEPT_FACE",FACE,{"disambiguationData":[OSD([sQuery(id+"F1.wireOp",EDGE,"E52.MirrorCS")])]}),makeQuery(id+"F6.opExtrude","SWEPT_FACE",FACE,{"disambiguationData":[OSD([sQuery(id+"F1.wireOp",EDGE,"E56.MirrorCS")])]}),makeQuery(id+"F6.opExtrude","SWEPT_FACE",FACE,{"disambiguationData":[OSD([sQuery(id+"F1.wireOp",EDGE,"E61.MirrorCS")])]}),makeQuery(id+"F6.opExtrude","SWEPT_FACE",FACE,{"disambiguationData":[OSD([sQuery(id+"F1.wireOp",EDGE,"E65.MirrorCS")])]}),makeQuery(id+"F6.opExtrude","SWEPT_FACE",FACE,{"disambiguationData":[OSD([sQuery(id+"F1.wireOp",EDGE,"E66.MirrorCS")])]}),makeQuery(id+"F6.opExtrude","SWEPT_FACE",FACE,{"disambiguationData":[OSD([sQuery(id+"F1.wireOp",EDGE,"E68.MirrorCS")])]}),makeQuery(id+"F6.opExtrude","SWEPT_FACE",FACE,{"disambiguationData":[OSD([sQuery(id+"F1.wireOp",EDGE,"E77.MirrorCS")])]}),makeQuery(id+"F6.opExtrude","SWEPT_FACE",FACE,{"disambiguationData":[OSD([sQuery(id+"F1.wireOp",EDGE,"E82.MirrorCS")])]}),makeQuery(id+"F6.opExtrude","SWEPT_FACE",FACE,{"disambiguationData":[OSD([sQuery(id+"F1.wireOp",EDGE,"3edb70b5-b804-4be9-ab85-b3a438d212921.MirrorCS")])]}),makeQuery(id+"F6.opExtrude","SWEPT_FACE",FACE,{"disambiguationData":[OSD([sQuery(id+"F1.wireOp",EDGE,"3edb70b5-b804-4be9-ab85-b3a438d212922.MirrorCS")])]}),makeQuery(id+"F6.opExtrude","SWEPT_FACE",FACE,{"disambiguationData":[OSD([sQuery(id+"F1.wireOp",EDGE,"3edb70b5-b804-4be9-ab85-b3a438d212923.MirrorCS")])]}),makeQuery(id+"F6.opExtrude","SWEPT_FACE",FACE,{"disambiguationData":[OSD([sQuery(id+"F1.wireOp",EDGE,"3edb70b5-b804-4be9-ab85-b3a438d212927.MirrorCS")])]}),makeQuery(id+"F6.opExtrude","SWEPT_FACE",FACE,{"disambiguationData":[OSD([sQuery(id+"F1.wireOp",EDGE,"3edb70b5-b804-4be9-ab85-b3a438d2129211.MirrorCS")])]}),makeQuery(id+"F6.opExtrude","SWEPT_FACE",FACE,{"disambiguationData":[OSD([sQuery(id+"F1.wireOp",EDGE,"3edb70b5-b804-4be9-ab85-b3a438d2129214.MirrorCS")])]}),makeQuery(id+"F6.opExtrude","SWEPT_FACE",FACE,{"disambiguationData":[OSD([sQuery(id+"F1.wireOp",EDGE,"3edb70b5-b804-4be9-ab85-b3a438d2129215.MirrorCS")])]}),makeQuery(id+"F6.opExtrude","SWEPT_FACE",FACE,{"disambiguationData":[OSD([sQuery(id+"F1.wireOp",EDGE,"3edb70b5-b804-4be9-ab85-b3a438d2129216.MirrorCS")])]}),makeQuery(id+"F6.opExtrude","SWEPT_FACE",FACE,{"disambiguationData":[OSD([sQuery(id+"F1.wireOp",EDGE,"3edb70b5-b804-4be9-ab85-b3a438d2129218.MirrorCS")])]}),makeQuery(id+"F6.opExtrude","SWEPT_FACE",FACE,{"disambiguationData":[OSD([sQuery(id+"F1.wireOp",EDGE,"3edb70b5-b804-4be9-ab85-b3a438d2129220.MirrorCS")])]}),makeQuery(id+"F6.opExtrude","SWEPT_FACE",FACE,{"disambiguationData":[OSD([sQuery(id+"F1.wireOp",EDGE,"3edb70b5-b804-4be9-ab85-b3a438d2129225.MirrorCS")])]}),makeQuery(id+"F6.opExtrude","SWEPT_FACE",FACE,{"disambiguationData":[OSD([sQuery(id+"F1.wireOp",EDGE,"3edb70b5-b804-4be9-ab85-b3a438d2129226.MirrorCS")])]}),makeQuery(id+"F6.opExtrude","SWEPT_FACE",FACE,{"disambiguationData":[OSD([sQuery(id+"F1.wireOp",EDGE,"3edb70b5-b804-4be9-ab85-b3a438d2129233.MirrorCS")])]}),makeQuery(id+"F6.opExtrude","SWEPT_FACE",FACE,{"disambiguationData":[OSD([sQuery(id+"F1.wireOp",EDGE,"3edb70b5-b804-4be9-ab85-b3a438d2129246.MirrorCS")])]}),makeQuery(id+"F6.opExtrude","SWEPT_FACE",FACE,{"disambiguationData":[OSD([sQuery(id+"F1.wireOp",EDGE,"3edb70b5-b804-4be9-ab85-b3a438d2129262.MirrorCS")])]}),makeQuery(id+"F6.opExtrude","SWEPT_FACE",FACE,{"disambiguationData":[OSD([sQuery(id+"F1.wireOp",EDGE,"3edb70b5-b804-4be9-ab85-b3a438d2129264.MirrorCS")])]}),makeQuery(id+"F6.opExtrude","SWEPT_FACE",FACE,{"disambiguationData":[OSD([sQuery(id+"F1.wireOp",EDGE,"3edb70b5-b804-4be9-ab85-b3a438d2129271.MirrorCS")])]}),makeQuery(id+"F6.opExtrude","SWEPT_FACE",FACE,{"disambiguationData":[OSD([sQuery(id+"F1.wireOp",EDGE,"3edb70b5-b804-4be9-ab85-b3a438d2129284.MirrorCS")])]}),makeQuery(id+"F6.opExtrude","SWEPT_FACE",FACE,{"disambiguationData":[OSD([sQuery(id+"F1.wireOp",EDGE,"14cc3a12-7d66-4c02-94a9-419769d572550.MirrorCS")])]}),makeQuery(id+"F6.opExtrude","SWEPT_FACE",FACE,{"disambiguationData":[OSD([sQuery(id+"F1.wireOp",EDGE,"14cc3a12-7d66-4c02-94a9-419769d572553.MirrorCS")])]}),makeQuery(id+"F6.opExtrude","SWEPT_FACE",FACE,{"disambiguationData":[OSD([sQuery(id+"F1.wireOp",EDGE,"14cc3a12-7d66-4c02-94a9-419769d572557.MirrorCS")])]}),makeQuery(id+"F6.opExtrude","SWEPT_FACE",FACE,{"disambiguationData":[OSD([sQuery(id+"F1.wireOp",EDGE,"14cc3a12-7d66-4c02-94a9-419769d572558.MirrorCS")])]}),makeQuery(id+"F6.opExtrude","SWEPT_FACE",FACE,{"disambiguationData":[OSD([sQuery(id+"F1.wireOp",EDGE,"14cc3a12-7d66-4c02-94a9-419769d5725512.MirrorCS")])]}),makeQuery(id+"F6.opExtrude","SWEPT_FACE",FACE,{"disambiguationData":[OSD([sQuery(id+"F1.wireOp",EDGE,"14cc3a12-7d66-4c02-94a9-419769d5725514.MirrorCS")])]}),makeQuery(id+"F6.opExtrude","SWEPT_FACE",FACE,{"disambiguationData":[OSD([sQuery(id+"F1.wireOp",EDGE,"14cc3a12-7d66-4c02-94a9-419769d5725515.MirrorCS")])]}),makeQuery(id+"F6.opExtrude","SWEPT_FACE",FACE,{"disambiguationData":[OSD([sQuery(id+"F1.wireOp",EDGE,"14cc3a12-7d66-4c02-94a9-419769d5725517.MirrorCS")])]}),makeQuery(id+"F6.opExtrude","SWEPT_FACE",FACE,{"disambiguationData":[OSD([sQuery(id+"F1.wireOp",EDGE,"14cc3a12-7d66-4c02-94a9-419769d5725522.MirrorCS")])]}),makeQuery(id+"F6.opExtrude","SWEPT_FACE",FACE,{"disambiguationData":[OSD([sQuery(id+"F1.wireOp",EDGE,"14cc3a12-7d66-4c02-94a9-419769d5725531.MirrorCS")])]}),makeQuery(id+"F6.opExtrude","SWEPT_FACE",FACE,{"disambiguationData":[OSD([sQuery(id+"F1.wireOp",EDGE,"14cc3a12-7d66-4c02-94a9-419769d5725540.MirrorCS")])]}),makeQuery(id+"F6.opExtrude","SWEPT_FACE",FACE,{"disambiguationData":[OSD([sQuery(id+"F1.wireOp",EDGE,"14cc3a12-7d66-4c02-94a9-419769d5725550.MirrorCS")])]}),makeQuery(id+"F6.opExtrude","SWEPT_FACE",FACE,{"disambiguationData":[OSD([sQuery(id+"F1.wireOp",EDGE,"E90.top")])]}),makeQuery(id+"F6.opExtrude","SWEPT_FACE",FACE,{"disambiguationData":[OSD([sQuery(id+"F1.wireOp",EDGE,"E91.top")])]}),makeQuery(id+"F6.opExtrude","SWEPT_FACE",FACE,{"disambiguationData":[OSD([sQuery(id+"F1.wireOp",EDGE,"d6889f29-3aff-4a43-887b-f05846102f70.top")])]}),makeQuery(id+"F6.opExtrude","SWEPT_FACE",FACE,{"disambiguationData":[OSD([sQuery(id+"F1.wireOp",EDGE,"767c3735-2e18-495c-a88c-5e601239b8bc.top")])]}),makeQuery(id+"F6.opExtrude","SWEPT_FACE",FACE,{"disambiguationData":[OSD([sQuery(id+"F1.wireOp",EDGE,"edaeaa6a-4a46-43e7-a4a8-70bf9d0c2d230.MirrorCS")])]}),makeQuery(id+"F6.opExtrude","SWEPT_FACE",FACE,{"disambiguationData":[OSD([sQuery(id+"F1.wireOp",EDGE,"6148efe5-7769-4a6e-beb2-6f02e7a2884e0.MirrorCS")])]}),makeQuery(id+"F6.opExtrude","SWEPT_FACE",FACE,{"disambiguationData":[OSD([sQuery(id+"F1.wireOp",EDGE,"498a5576-9314-4d20-a76d-96ff3a6abcc60.MirrorCS")])]}),makeQuery(id+"F6.opExtrude","SWEPT_FACE",FACE,{"disambiguationData":[OSD([sQuery(id+"F1.wireOp",EDGE,"2b8ea9ff-144e-4082-a664-a4dd3dd94e410.MirrorCS")])]}),makeQuery(id+"F6.opExtrude","SWEPT_FACE",FACE,{"disambiguationData":[OSD([sQuery(id+"F1.wireOp",EDGE,"55912813-85c1-4332-9b60-ee472111f4600.MirrorCS")])]})]});
            var sketch = newSketch(context, id + "F7", { "sketchPlane" : qUnion([Q0])});
            skLineSegment(sketch, "E96.bottom", {"start": v(0, 20) * mm, "end": v(3, 20) * mm});
            skLineSegment(sketch, "E96.top", {"start": v(0, 6) * mm, "end": v(3, 6) * mm});
            skLineSegment(sketch, "E96.left", {"start": v(0, 20) * mm, "end": v(0, 6) * mm});
            skLineSegment(sketch, "E96.right", {"start": v(3, 20) * mm, "end": v(3, 6) * mm});
            skLineSegment(sketch, "E97.bottom", {"start": v(42.6, 20) * mm, "end": v(45.6, 20) * mm});
            skLineSegment(sketch, "E97.top", {"start": v(42.6, 6) * mm, "end": v(45.6, 6) * mm});
            skLineSegment(sketch, "E97.left", {"start": v(42.6, 20) * mm, "end": v(42.6, 6) * mm});
            skLineSegment(sketch, "E97.right", {"start": v(45.6, 20) * mm, "end": v(45.6, 6) * mm});
            skLineSegment(sketch, "E98.bottom", {"start": v(87.05, 20) * mm, "end": v(90.05, 20) * mm});
            skLineSegment(sketch, "E98.top", {"start": v(87.05, 6) * mm, "end": v(90.05, 6) * mm});
            skLineSegment(sketch, "E98.left", {"start": v(87.05, 20) * mm, "end": v(87.05, 6) * mm});
            skLineSegment(sketch, "E98.right", {"start": v(90.05, 20) * mm, "end": v(90.05, 6) * mm});
            skPoint(sketch, "E99", {"position": v(44.1, 6) * mm});
            skPoint(sketch, "E100", {"position": v(88.55, 6) * mm});
            skLineSegment(sketch, "E101.MirrorCS", {"start": v(132.65, 6) * mm, "end": v(129.65, 6) * mm});
            skLineSegment(sketch, "E102.MirrorCS", {"start": v(132.65, 20) * mm, "end": v(129.65, 20) * mm});
            skLineSegment(sketch, "E103", {"start": v(0, 14) * mm, "end": v(3, 14) * mm});
            skLineSegment(sketch, "E104.trimOffspring", {"start": v(129.65, 14) * mm, "end": v(132.65, 14) * mm});
            skLineSegment(sketch, "E105.trimOffspring", {"start": v(42.6, 14) * mm, "end": v(45.6, 14) * mm});
            skLineSegment(sketch, "E106.trimOffspring", {"start": v(87.05, 14) * mm, "end": v(90.05, 14) * mm});
            skLineSegment(sketch, "E107", {"start": v(129.65, 6) * mm, "end": v(129.65, 20) * mm});
            skSolve(sketch);
        }
        {
            var Q0;
            {var subQ2=sQuery(id+"F7.wireOp",EDGE,"2fbbb86d-52ca-4042-bc13-ee66f33171935.MirrorCS");Q0=makeQuery(id+"F7.imprint","IMPRINT",FACE,{"disambiguationData":[TD([[makeQuery(id+"F7.imprint","IMPRINT",EDGE,{"derivedFrom":subQ2}),-1.0]])]});}
            var Q1;
            {var subQ2=sQuery(id+"F7.wireOp",EDGE,"2fbbb86d-52ca-4042-bc13-ee66f33171930.MirrorCS");Q1=makeQuery(id+"F7.imprint","IMPRINT",FACE,{"disambiguationData":[TD([[makeQuery(id+"F7.imprint","IMPRINT",EDGE,{"derivedFrom":subQ2}),-1.0]])]});}
            var Q2;
            {var subQ2=sQuery(id+"F7.wireOp",EDGE,"E101.MirrorCS");Q2=makeQuery(id+"F7.imprint","IMPRINT",FACE,{"disambiguationData":[TD([[makeQuery(id+"F7.imprint","IMPRINT",EDGE,{"derivedFrom":subQ2}),-1.0]])]});}
            var Q3;
            {var subQ2=sQuery(id+"F7.wireOp",EDGE,"2fbbb86d-52ca-4042-bc13-ee66f33171931.MirrorCS");Q3=makeQuery(id+"F7.imprint","IMPRINT",FACE,{"disambiguationData":[TD([[makeQuery(id+"F7.imprint","IMPRINT",EDGE,{"derivedFrom":subQ2}),-1.0]])]});}
            var Q4;
            {var subQ2=sQuery(id+"F7.wireOp",EDGE,"E97.top");Q4=makeQuery(id+"F7.imprint","IMPRINT",FACE,{"disambiguationData":[TD([[makeQuery(id+"F7.imprint","IMPRINT",EDGE,{"derivedFrom":subQ2}),1.0]])]});}
            var Q5;
            {var subQ2=sQuery(id+"F7.wireOp",EDGE,"E96.top");Q5=makeQuery(id+"F7.imprint","IMPRINT",FACE,{"disambiguationData":[TD([[makeQuery(id+"F7.imprint","IMPRINT",EDGE,{"derivedFrom":subQ2}),1.0]])]});}
            var Q6;
            {var subQ2=sQuery(id+"F7.wireOp",EDGE,"E98.top");Q6=makeQuery(id+"F7.imprint","IMPRINT",FACE,{"disambiguationData":[TD([[makeQuery(id+"F7.imprint","IMPRINT",EDGE,{"derivedFrom":subQ2}),1.0]])]});}
            var Q7;
            {var subQ2=sQuery(id+"F7.wireOp",EDGE,"e348e82e-9c53-4cde-95ef-f9083b8c8da1.top");Q7=makeQuery(id+"F7.imprint","IMPRINT",FACE,{"disambiguationData":[TD([[makeQuery(id+"F7.imprint","IMPRINT",EDGE,{"derivedFrom":subQ2}),1.0]])]});}
            var Q8;
            {var subQ2=sQuery(id+"F7.wireOp",EDGE,"8fabef1b-b716-437d-b3f6-22a7b8f8532e.top");Q8=makeQuery(id+"F7.imprint","IMPRINT",FACE,{"disambiguationData":[TD([[makeQuery(id+"F7.imprint","IMPRINT",EDGE,{"derivedFrom":subQ2}),1.0]])]});}
            extrude(context, id + "F8", {"entities" : qUnion([Q0, Q1, Q2, Q3, Q4, Q5, Q6, Q7, Q8]), "operationType" : NewBodyOperationType.REMOVE, "endBound" : BoundingType.THROUGH_ALL, "oppositeDirection" : true, "depth" : 25 * mm});
        }
        {
            var Q0;
            Q0=makeQuery(id+"F0.imprint","IMPRINT",FACE,{"disambiguationData":[TD([[makeQuery(id+"F0.imprint","IMPRINT",EDGE,{"derivedFrom":sQuery(id+"F0.wireOp",EDGE,"E0.bottom")}),1.0]])]});
            var sketch = newSketch(context, id + "F9", { "sketchPlane" : qUnion([Q0])});
            skLineSegment(sketch, "E108.MirrorCS", {"start": v(129.65, 9) * mm, "end": v(132.65, 9) * mm});
            skLineSegment(sketch, "E109.MirrorCS", {"start": v(129.65, 12) * mm, "end": v(129.65, 9) * mm});
            skLineSegment(sketch, "E110.MirrorCS", {"start": v(129.65, 12) * mm, "end": v(132.65, 12) * mm});
            skLineSegment(sketch, "E111.MirrorCS", {"start": v(87.05, 12) * mm, "end": v(87.05, 9) * mm});
            skLineSegment(sketch, "E112.MirrorCS", {"start": v(87.05, 12) * mm, "end": v(90.05, 12) * mm});
            skLineSegment(sketch, "E113.MirrorCS", {"start": v(42.6, 9) * mm, "end": v(45.6, 9) * mm});
            skLineSegment(sketch, "E114.MirrorCS", {"start": v(45.6, 12) * mm, "end": v(45.6, 9) * mm});
            skLineSegment(sketch, "E115.MirrorCS", {"start": v(42.6, 12) * mm, "end": v(45.6, 12) * mm});
            skLineSegment(sketch, "E116.MirrorCS", {"start": v(132.65, 12) * mm, "end": v(132.65, 9) * mm});
            skLineSegment(sketch, "E117.MirrorCS", {"start": v(90.05, 12) * mm, "end": v(90.05, 9) * mm});
            skLineSegment(sketch, "E118.MirrorCS", {"start": v(87.05, 9) * mm, "end": v(90.05, 9) * mm});
            skLineSegment(sketch, "E119.MirrorCS", {"start": v(42.6, 12) * mm, "end": v(42.6, 9) * mm});
            skPoint(sketch, "E120.MirrorP", {"position": v(88.55, 12) * mm});
            skPoint(sketch, "E121.MirrorP", {"position": v(44.1, 12) * mm});
            skLineSegment(sketch, "E122.bottom", {"start": v(0, 12) * mm, "end": v(3, 12) * mm});
            skLineSegment(sketch, "E122.top", {"start": v(0, 9) * mm, "end": v(3, 9) * mm});
            skLineSegment(sketch, "E122.left", {"start": v(0, 12) * mm, "end": v(0, 9) * mm});
            skLineSegment(sketch, "E122.right", {"start": v(3, 12) * mm, "end": v(3, 9) * mm});
            skSolve(sketch);
        }
        {
            var Q0;
            Q0=makeQuery(id+"F9.imprint","IMPRINT",FACE,{"disambiguationData":[TD([[makeQuery(id+"F9.imprint","IMPRINT",EDGE,{"derivedFrom":sQuery(id+"F9.wireOp",EDGE,"5a775dd9-6bc8-473d-95ec-c2d6bb1f0a98.bottom")}),-1.0]])]});
            var Q1;
            Q1=makeQuery(id+"F9.imprint","IMPRINT",FACE,{"disambiguationData":[TD([[makeQuery(id+"F9.imprint","IMPRINT",EDGE,{"derivedFrom":sQuery(id+"F9.wireOp",EDGE,"8be4bab3-1352-4574-9c24-f700de786d43.bottom")}),-1.0]])]});
            var Q2;
            Q2=makeQuery(id+"F9.imprint","IMPRINT",FACE,{"disambiguationData":[TD([[makeQuery(id+"F9.imprint","IMPRINT",EDGE,{"derivedFrom":sQuery(id+"F9.wireOp",EDGE,"2998de47-cd87-4efd-afcf-3869d960d94d.bottom")}),-1.0]])]});
            var Q3;
            Q3=makeQuery(id+"F9.imprint","IMPRINT",FACE,{"disambiguationData":[TD([[makeQuery(id+"F9.imprint","IMPRINT",EDGE,{"derivedFrom":sQuery(id+"F9.wireOp",EDGE,"91a61f26-1a3f-4266-a8f7-8f5f60bf52a4.bottom")}),-1.0]])]});
            var Q4;
            Q4=makeQuery(id+"F9.imprint","IMPRINT",FACE,{"disambiguationData":[TD([[makeQuery(id+"F9.imprint","IMPRINT",EDGE,{"derivedFrom":sQuery(id+"F9.wireOp",EDGE,"E111.MirrorCS")}),1.0]])]});
            var Q5;
            Q5=makeQuery(id+"F9.imprint","IMPRINT",FACE,{"disambiguationData":[TD([[makeQuery(id+"F9.imprint","IMPRINT",EDGE,{"derivedFrom":sQuery(id+"F9.wireOp",EDGE,"E108.MirrorCS")}),1.0]])]});
            var Q6;
            Q6=makeQuery(id+"F9.imprint","IMPRINT",FACE,{"disambiguationData":[TD([[makeQuery(id+"F9.imprint","IMPRINT",EDGE,{"derivedFrom":sQuery(id+"F9.wireOp",EDGE,"ad72ea87-a3ef-4f9b-bd59-e7783f2f5778.bottom")}),-1.0]])]});
            var Q7;
            Q7=makeQuery(id+"F9.imprint","IMPRINT",FACE,{"disambiguationData":[TD([[makeQuery(id+"F9.imprint","IMPRINT",EDGE,{"derivedFrom":sQuery(id+"F9.wireOp",EDGE,"E113.MirrorCS")}),1.0]])]});
            var Q8;
            Q8=makeQuery(id+"F9.imprint","IMPRINT",FACE,{"disambiguationData":[TD([[makeQuery(id+"F9.imprint","IMPRINT",EDGE,{"derivedFrom":sQuery(id+"F9.wireOp",EDGE,"de8f891b-2fd5-4b08-8b68-09a0fd3303620.MirrorCS")}),-1.0]])]});
            var Q9;
            Q9=makeQuery(id+"F9.imprint","IMPRINT",FACE,{"disambiguationData":[TD([[makeQuery(id+"F9.imprint","IMPRINT",EDGE,{"derivedFrom":sQuery(id+"F9.wireOp",EDGE,"E122.bottom")}),-1.0]])]});
            extrude(context, id + "F10", {"entities" : qUnion([Q0, Q1, Q2, Q3, Q4, Q5, Q6, Q7, Q8, Q9]), "operationType" : NewBodyOperationType.REMOVE, "endBound" : BoundingType.THROUGH_ALL, "depth" : 25 * mm});
        }
        {
            var Q0;
            Q0=makeQuery(id+"F6.boolean.opBoolean","MERGE",FACE,{"derivedFrom":[makeQuery(id+"F5.opExtrude","SWEPT_FACE",FACE,{"disambiguationData":[OSD([sQuery(id+"F2.wireOp",EDGE,"E95.top")])]}),makeQuery(id+"F6.opExtrude","SWEPT_FACE",FACE,{"disambiguationData":[OSD([sQuery(id+"F1.wireOp",EDGE,"E18.top")])]}),makeQuery(id+"F6.opExtrude","SWEPT_FACE",FACE,{"disambiguationData":[OSD([sQuery(id+"F1.wireOp",EDGE,"E19.top")])]}),makeQuery(id+"F6.opExtrude","SWEPT_FACE",FACE,{"disambiguationData":[OSD([sQuery(id+"F1.wireOp",EDGE,"E20.top")])]}),makeQuery(id+"F6.opExtrude","SWEPT_FACE",FACE,{"disambiguationData":[OSD([sQuery(id+"F1.wireOp",EDGE,"E23.top")])]}),makeQuery(id+"F6.opExtrude","SWEPT_FACE",FACE,{"disambiguationData":[OSD([sQuery(id+"F1.wireOp",EDGE,"E24.top")])]}),makeQuery(id+"F6.opExtrude","SWEPT_FACE",FACE,{"disambiguationData":[OSD([sQuery(id+"F1.wireOp",EDGE,"E25.top")])]}),makeQuery(id+"F6.opExtrude","SWEPT_FACE",FACE,{"disambiguationData":[OSD([sQuery(id+"F1.wireOp",EDGE,"E37.MirrorCS")])]}),makeQuery(id+"F6.opExtrude","SWEPT_FACE",FACE,{"disambiguationData":[OSD([sQuery(id+"F1.wireOp",EDGE,"E47.MirrorCS")])]}),makeQuery(id+"F6.opExtrude","SWEPT_FACE",FACE,{"disambiguationData":[OSD([sQuery(id+"F1.wireOp",EDGE,"E48.MirrorCS")])]}),makeQuery(id+"F6.opExtrude","SWEPT_FACE",FACE,{"disambiguationData":[OSD([sQuery(id+"F1.wireOp",EDGE,"E50.MirrorCS")])]}),makeQuery(id+"F6.opExtrude","SWEPT_FACE",FACE,{"disambiguationData":[OSD([sQuery(id+"F1.wireOp",EDGE,"E52.MirrorCS")])]}),makeQuery(id+"F6.opExtrude","SWEPT_FACE",FACE,{"disambiguationData":[OSD([sQuery(id+"F1.wireOp",EDGE,"E56.MirrorCS")])]}),makeQuery(id+"F6.opExtrude","SWEPT_FACE",FACE,{"disambiguationData":[OSD([sQuery(id+"F1.wireOp",EDGE,"E61.MirrorCS")])]}),makeQuery(id+"F6.opExtrude","SWEPT_FACE",FACE,{"disambiguationData":[OSD([sQuery(id+"F1.wireOp",EDGE,"E65.MirrorCS")])]}),makeQuery(id+"F6.opExtrude","SWEPT_FACE",FACE,{"disambiguationData":[OSD([sQuery(id+"F1.wireOp",EDGE,"E66.MirrorCS")])]}),makeQuery(id+"F6.opExtrude","SWEPT_FACE",FACE,{"disambiguationData":[OSD([sQuery(id+"F1.wireOp",EDGE,"E68.MirrorCS")])]}),makeQuery(id+"F6.opExtrude","SWEPT_FACE",FACE,{"disambiguationData":[OSD([sQuery(id+"F1.wireOp",EDGE,"E77.MirrorCS")])]}),makeQuery(id+"F6.opExtrude","SWEPT_FACE",FACE,{"disambiguationData":[OSD([sQuery(id+"F1.wireOp",EDGE,"E82.MirrorCS")])]}),makeQuery(id+"F6.opExtrude","SWEPT_FACE",FACE,{"disambiguationData":[OSD([sQuery(id+"F1.wireOp",EDGE,"3edb70b5-b804-4be9-ab85-b3a438d212921.MirrorCS")])]}),makeQuery(id+"F6.opExtrude","SWEPT_FACE",FACE,{"disambiguationData":[OSD([sQuery(id+"F1.wireOp",EDGE,"3edb70b5-b804-4be9-ab85-b3a438d212922.MirrorCS")])]}),makeQuery(id+"F6.opExtrude","SWEPT_FACE",FACE,{"disambiguationData":[OSD([sQuery(id+"F1.wireOp",EDGE,"3edb70b5-b804-4be9-ab85-b3a438d212923.MirrorCS")])]}),makeQuery(id+"F6.opExtrude","SWEPT_FACE",FACE,{"disambiguationData":[OSD([sQuery(id+"F1.wireOp",EDGE,"3edb70b5-b804-4be9-ab85-b3a438d212927.MirrorCS")])]}),makeQuery(id+"F6.opExtrude","SWEPT_FACE",FACE,{"disambiguationData":[OSD([sQuery(id+"F1.wireOp",EDGE,"3edb70b5-b804-4be9-ab85-b3a438d2129211.MirrorCS")])]}),makeQuery(id+"F6.opExtrude","SWEPT_FACE",FACE,{"disambiguationData":[OSD([sQuery(id+"F1.wireOp",EDGE,"3edb70b5-b804-4be9-ab85-b3a438d2129214.MirrorCS")])]}),makeQuery(id+"F6.opExtrude","SWEPT_FACE",FACE,{"disambiguationData":[OSD([sQuery(id+"F1.wireOp",EDGE,"3edb70b5-b804-4be9-ab85-b3a438d2129215.MirrorCS")])]}),makeQuery(id+"F6.opExtrude","SWEPT_FACE",FACE,{"disambiguationData":[OSD([sQuery(id+"F1.wireOp",EDGE,"3edb70b5-b804-4be9-ab85-b3a438d2129216.MirrorCS")])]}),makeQuery(id+"F6.opExtrude","SWEPT_FACE",FACE,{"disambiguationData":[OSD([sQuery(id+"F1.wireOp",EDGE,"3edb70b5-b804-4be9-ab85-b3a438d2129218.MirrorCS")])]}),makeQuery(id+"F6.opExtrude","SWEPT_FACE",FACE,{"disambiguationData":[OSD([sQuery(id+"F1.wireOp",EDGE,"3edb70b5-b804-4be9-ab85-b3a438d2129220.MirrorCS")])]}),makeQuery(id+"F6.opExtrude","SWEPT_FACE",FACE,{"disambiguationData":[OSD([sQuery(id+"F1.wireOp",EDGE,"3edb70b5-b804-4be9-ab85-b3a438d2129225.MirrorCS")])]}),makeQuery(id+"F6.opExtrude","SWEPT_FACE",FACE,{"disambiguationData":[OSD([sQuery(id+"F1.wireOp",EDGE,"3edb70b5-b804-4be9-ab85-b3a438d2129226.MirrorCS")])]}),makeQuery(id+"F6.opExtrude","SWEPT_FACE",FACE,{"disambiguationData":[OSD([sQuery(id+"F1.wireOp",EDGE,"3edb70b5-b804-4be9-ab85-b3a438d2129233.MirrorCS")])]}),makeQuery(id+"F6.opExtrude","SWEPT_FACE",FACE,{"disambiguationData":[OSD([sQuery(id+"F1.wireOp",EDGE,"3edb70b5-b804-4be9-ab85-b3a438d2129246.MirrorCS")])]}),makeQuery(id+"F6.opExtrude","SWEPT_FACE",FACE,{"disambiguationData":[OSD([sQuery(id+"F1.wireOp",EDGE,"3edb70b5-b804-4be9-ab85-b3a438d2129262.MirrorCS")])]}),makeQuery(id+"F6.opExtrude","SWEPT_FACE",FACE,{"disambiguationData":[OSD([sQuery(id+"F1.wireOp",EDGE,"3edb70b5-b804-4be9-ab85-b3a438d2129264.MirrorCS")])]}),makeQuery(id+"F6.opExtrude","SWEPT_FACE",FACE,{"disambiguationData":[OSD([sQuery(id+"F1.wireOp",EDGE,"3edb70b5-b804-4be9-ab85-b3a438d2129271.MirrorCS")])]}),makeQuery(id+"F6.opExtrude","SWEPT_FACE",FACE,{"disambiguationData":[OSD([sQuery(id+"F1.wireOp",EDGE,"3edb70b5-b804-4be9-ab85-b3a438d2129284.MirrorCS")])]}),makeQuery(id+"F6.opExtrude","SWEPT_FACE",FACE,{"disambiguationData":[OSD([sQuery(id+"F1.wireOp",EDGE,"14cc3a12-7d66-4c02-94a9-419769d572550.MirrorCS")])]}),makeQuery(id+"F6.opExtrude","SWEPT_FACE",FACE,{"disambiguationData":[OSD([sQuery(id+"F1.wireOp",EDGE,"14cc3a12-7d66-4c02-94a9-419769d572553.MirrorCS")])]}),makeQuery(id+"F6.opExtrude","SWEPT_FACE",FACE,{"disambiguationData":[OSD([sQuery(id+"F1.wireOp",EDGE,"14cc3a12-7d66-4c02-94a9-419769d572557.MirrorCS")])]}),makeQuery(id+"F6.opExtrude","SWEPT_FACE",FACE,{"disambiguationData":[OSD([sQuery(id+"F1.wireOp",EDGE,"14cc3a12-7d66-4c02-94a9-419769d572558.MirrorCS")])]}),makeQuery(id+"F6.opExtrude","SWEPT_FACE",FACE,{"disambiguationData":[OSD([sQuery(id+"F1.wireOp",EDGE,"14cc3a12-7d66-4c02-94a9-419769d5725512.MirrorCS")])]}),makeQuery(id+"F6.opExtrude","SWEPT_FACE",FACE,{"disambiguationData":[OSD([sQuery(id+"F1.wireOp",EDGE,"14cc3a12-7d66-4c02-94a9-419769d5725514.MirrorCS")])]}),makeQuery(id+"F6.opExtrude","SWEPT_FACE",FACE,{"disambiguationData":[OSD([sQuery(id+"F1.wireOp",EDGE,"14cc3a12-7d66-4c02-94a9-419769d5725515.MirrorCS")])]}),makeQuery(id+"F6.opExtrude","SWEPT_FACE",FACE,{"disambiguationData":[OSD([sQuery(id+"F1.wireOp",EDGE,"14cc3a12-7d66-4c02-94a9-419769d5725517.MirrorCS")])]}),makeQuery(id+"F6.opExtrude","SWEPT_FACE",FACE,{"disambiguationData":[OSD([sQuery(id+"F1.wireOp",EDGE,"14cc3a12-7d66-4c02-94a9-419769d5725522.MirrorCS")])]}),makeQuery(id+"F6.opExtrude","SWEPT_FACE",FACE,{"disambiguationData":[OSD([sQuery(id+"F1.wireOp",EDGE,"14cc3a12-7d66-4c02-94a9-419769d5725531.MirrorCS")])]}),makeQuery(id+"F6.opExtrude","SWEPT_FACE",FACE,{"disambiguationData":[OSD([sQuery(id+"F1.wireOp",EDGE,"14cc3a12-7d66-4c02-94a9-419769d5725540.MirrorCS")])]}),makeQuery(id+"F6.opExtrude","SWEPT_FACE",FACE,{"disambiguationData":[OSD([sQuery(id+"F1.wireOp",EDGE,"14cc3a12-7d66-4c02-94a9-419769d5725550.MirrorCS")])]}),makeQuery(id+"F6.opExtrude","SWEPT_FACE",FACE,{"disambiguationData":[OSD([sQuery(id+"F1.wireOp",EDGE,"E90.top")])]}),makeQuery(id+"F6.opExtrude","SWEPT_FACE",FACE,{"disambiguationData":[OSD([sQuery(id+"F1.wireOp",EDGE,"E91.top")])]}),makeQuery(id+"F6.opExtrude","SWEPT_FACE",FACE,{"disambiguationData":[OSD([sQuery(id+"F1.wireOp",EDGE,"d6889f29-3aff-4a43-887b-f05846102f70.top")])]}),makeQuery(id+"F6.opExtrude","SWEPT_FACE",FACE,{"disambiguationData":[OSD([sQuery(id+"F1.wireOp",EDGE,"767c3735-2e18-495c-a88c-5e601239b8bc.top")])]}),makeQuery(id+"F6.opExtrude","SWEPT_FACE",FACE,{"disambiguationData":[OSD([sQuery(id+"F1.wireOp",EDGE,"edaeaa6a-4a46-43e7-a4a8-70bf9d0c2d230.MirrorCS")])]}),makeQuery(id+"F6.opExtrude","SWEPT_FACE",FACE,{"disambiguationData":[OSD([sQuery(id+"F1.wireOp",EDGE,"6148efe5-7769-4a6e-beb2-6f02e7a2884e0.MirrorCS")])]}),makeQuery(id+"F6.opExtrude","SWEPT_FACE",FACE,{"disambiguationData":[OSD([sQuery(id+"F1.wireOp",EDGE,"498a5576-9314-4d20-a76d-96ff3a6abcc60.MirrorCS")])]}),makeQuery(id+"F6.opExtrude","SWEPT_FACE",FACE,{"disambiguationData":[OSD([sQuery(id+"F1.wireOp",EDGE,"2b8ea9ff-144e-4082-a664-a4dd3dd94e410.MirrorCS")])]}),makeQuery(id+"F6.opExtrude","SWEPT_FACE",FACE,{"disambiguationData":[OSD([sQuery(id+"F1.wireOp",EDGE,"55912813-85c1-4332-9b60-ee472111f4600.MirrorCS")])]})]});
            var sketch = newSketch(context, id + "F11", { "sketchPlane" : qUnion([Q0])});
            skLineSegment(sketch, "E123", {"start": v(3, 6) * mm, "end": v(42.6, 6) * mm, "construction": true});
            skLineSegment(sketch, "E124", {"start": v(45.6, 6) * mm, "end": v(87.05, 6) * mm, "construction": true});
            skLineSegment(sketch, "E125", {"start": v(90.05, 6) * mm, "end": v(129.65, 6) * mm, "construction": true});
            skCircle(sketch, "E126", {"center": v(109.85, 14) * mm, "radius": 2 * mm});
            skPoint(sketch, "E126.centerSnap0", {"position": v(109.85, 6) * mm});
            skCircle(sketch, "E127", {"center": v(22.8, 14) * mm, "radius": 2 * mm});
            skPoint(sketch, "E127.centerSnap0", {"position": v(22.8, 6) * mm});
            skCircle(sketch, "E128", {"center": v(66.33, 6) * mm, "radius": 2 * mm});
            skSolve(sketch);
        }
        {
            var Q0;
            {var subQ0=sQuery(id+"F1.wireOp",EDGE,"E89.left");Q0=makeQuery(id+"F8.boolean.opBoolean","SPLIT",FACE,{"disambiguationData":[TD([makeQuery(id+"F8.opExtrude","SWEPT_FACE",FACE,{"disambiguationData":[OSD([sQuery(id+"F7.wireOp",EDGE,"E96.top")])]})])],"derivedFrom":makeQuery(id+"F6.boolean.opBoolean","MERGE",FACE,{"derivedFrom":[makeQuery(id+"F5.opExtrude","SWEPT_FACE",FACE,{"disambiguationData":[OSD([sQuery(id+"F2.wireOp",EDGE,"E95.left")])]}),makeQuery(id+"F6.opExtrude","SWEPT_FACE",FACE,{"disambiguationData":[OSD([subQ0])]})]})});}
            var sketch = newSketch(context, id + "F12", { "sketchPlane" : qUnion([Q0])});
            skLineSegment(sketch, "E129", {"start": v(-20, 3) * mm, "end": v(-20, 6) * mm});
            skLineSegment(sketch, "E130", {"start": v(-20, 6) * mm, "end": v(-3, 12) * mm});
            skLineSegment(sketch, "E131", {"start": v(3, 9) * mm, "end": v(3, 9) * mm});
            skLineSegment(sketch, "E132", {"start": v(3, 9) * mm, "end": v(0, 9) * mm});
            skLineSegment(sketch, "E133", {"start": v(0, 9) * mm, "end": v(0, 3) * mm});
            skLineSegment(sketch, "E134", {"start": v(0, 3) * mm, "end": v(-6, 3) * mm});
            skLineSegment(sketch, "E135", {"start": v(-6, 3) * mm, "end": v(-6, 0) * mm});
            skLineSegment(sketch, "E136", {"start": v(-6, 0) * mm, "end": v(-14, 0) * mm});
            skLineSegment(sketch, "E137", {"start": v(-14, 0) * mm, "end": v(-14, 3) * mm});
            skLineSegment(sketch, "E138", {"start": v(-14, 3) * mm, "end": v(-20, 3) * mm});
            skPoint(sketch, "E139.orphan", {"position": v(-20, 0) * mm});
            skLineSegment(sketch, "E140", {"start": v(3, 12) * mm, "end": v(-3, 12) * mm});
            skLineSegment(sketch, "E141", {"start": v(3, 9) * mm, "end": v(3, 12) * mm});
            skSolve(sketch);
        }
        {
            var Q0;
            Q0=makeQuery(id+"F11.imprint","IMPRINT",FACE,{"disambiguationData":[TD([[makeQuery(id+"F11.imprint","IMPRINT",EDGE,{"derivedFrom":sQuery(id+"F11.wireOp",EDGE,"94b2442c-a40f-45f4-8ef9-0b2a968136b4")}),1.0]])]});
            var Q1;
            Q1=makeQuery(id+"F11.imprint","IMPRINT",FACE,{"disambiguationData":[TD([[makeQuery(id+"F11.imprint","IMPRINT",EDGE,{"derivedFrom":sQuery(id+"F11.wireOp",EDGE,"a2ab44ba-30ad-4a2f-9bb6-ee1dff1c87a7")}),1.0]])]});
            var Q2;
            Q2=makeQuery(id+"F11.imprint","IMPRINT",FACE,{"disambiguationData":[TD([[makeQuery(id+"F11.imprint","IMPRINT",EDGE,{"derivedFrom":sQuery(id+"F11.wireOp",EDGE,"e37bc460-d82d-41b5-8908-47586745a7d3")}),1.0]])]});
            var Q3;
            {var subQ0=sQuery(id+"F11.wireOp",EDGE,"a39ae753-7805-4370-b947-9dffeaf50725");var subQ1=sQuery(id+"F11.wireOp",EDGE,"cf4042b7-3196-4cee-b34a-309d7e30c544");var subQ3=makeQuery(id+"F11.imprint","INTERSECT",VERTEX,{"disambiguationData":[OD(0.0)],"derivedFrom":[subQ1,subQ0]});Q3=makeQuery(id+"F11.imprint","IMPRINT",FACE,{"disambiguationData":[TD([[makeQuery(id+"F11.imprint","IMPRINT",EDGE,{"disambiguationData":[TD([[subQ3,-1.0]])],"derivedFrom":subQ1}),1.0]])]});}
            var Q4;
            {var subQ0=sQuery(id+"F11.wireOp",EDGE,"a39ae753-7805-4370-b947-9dffeaf50725");var subQ1=sQuery(id+"F11.wireOp",EDGE,"cf4042b7-3196-4cee-b34a-309d7e30c544");var subQ3=makeQuery(id+"F11.imprint","INTERSECT",VERTEX,{"disambiguationData":[OD(0.0)],"derivedFrom":[subQ1,subQ0]});Q4=makeQuery(id+"F11.imprint","IMPRINT",FACE,{"disambiguationData":[TD([[makeQuery(id+"F11.imprint","IMPRINT",EDGE,{"disambiguationData":[TD([[subQ3,-1.0]])],"derivedFrom":subQ1}),-1.0]])]});}
            var Q5;
            Q5=makeQuery(id+"F11.imprint","IMPRINT",FACE,{"disambiguationData":[TD([[makeQuery(id+"F11.imprint","IMPRINT",EDGE,{"derivedFrom":sQuery(id+"F11.wireOp",EDGE,"8381d837-c9fe-45d1-8590-3962efa3db3a")}),1.0]])]});
            var Q6;
            Q6=makeQuery(id+"F11.imprint","IMPRINT",FACE,{"disambiguationData":[TD([[makeQuery(id+"F11.imprint","IMPRINT",EDGE,{"derivedFrom":sQuery(id+"F11.wireOp",EDGE,"E128")}),1.0]])]});
            var Q7;
            Q7=makeQuery(id+"F11.imprint","IMPRINT",FACE,{"disambiguationData":[TD([[makeQuery(id+"F11.imprint","IMPRINT",EDGE,{"derivedFrom":sQuery(id+"F11.wireOp",EDGE,"E126")}),1.0]])]});
            var Q8;
            Q8=makeQuery(id+"F11.imprint","IMPRINT",FACE,{"disambiguationData":[TD([[makeQuery(id+"F11.imprint","IMPRINT",EDGE,{"derivedFrom":sQuery(id+"F11.wireOp",EDGE,"E127")}),1.0]])]});
            extrude(context, id + "F13", {"entities" : qUnion([Q0, Q1, Q2, Q3, Q4, Q5, Q6, Q7, Q8]), "operationType" : NewBodyOperationType.REMOVE, "endBound" : BoundingType.THROUGH_ALL, "oppositeDirection" : true, "depth" : 25 * mm});
        }
        {
            var Q0;
            Q0=makeQuery(id+"F12.imprint","IMPRINT",FACE,{"disambiguationData":[TD([[makeQuery(id+"F12.imprint","IMPRINT",EDGE,{"derivedFrom":sQuery(id+"F12.wireOp",EDGE,"E129")}),-1.0]])]});
            extrude(context, id + "F14", {"entities" : qUnion([Q0]), "oppositeDirection" : true, "depth" : 3 * mm});
        }
    });
